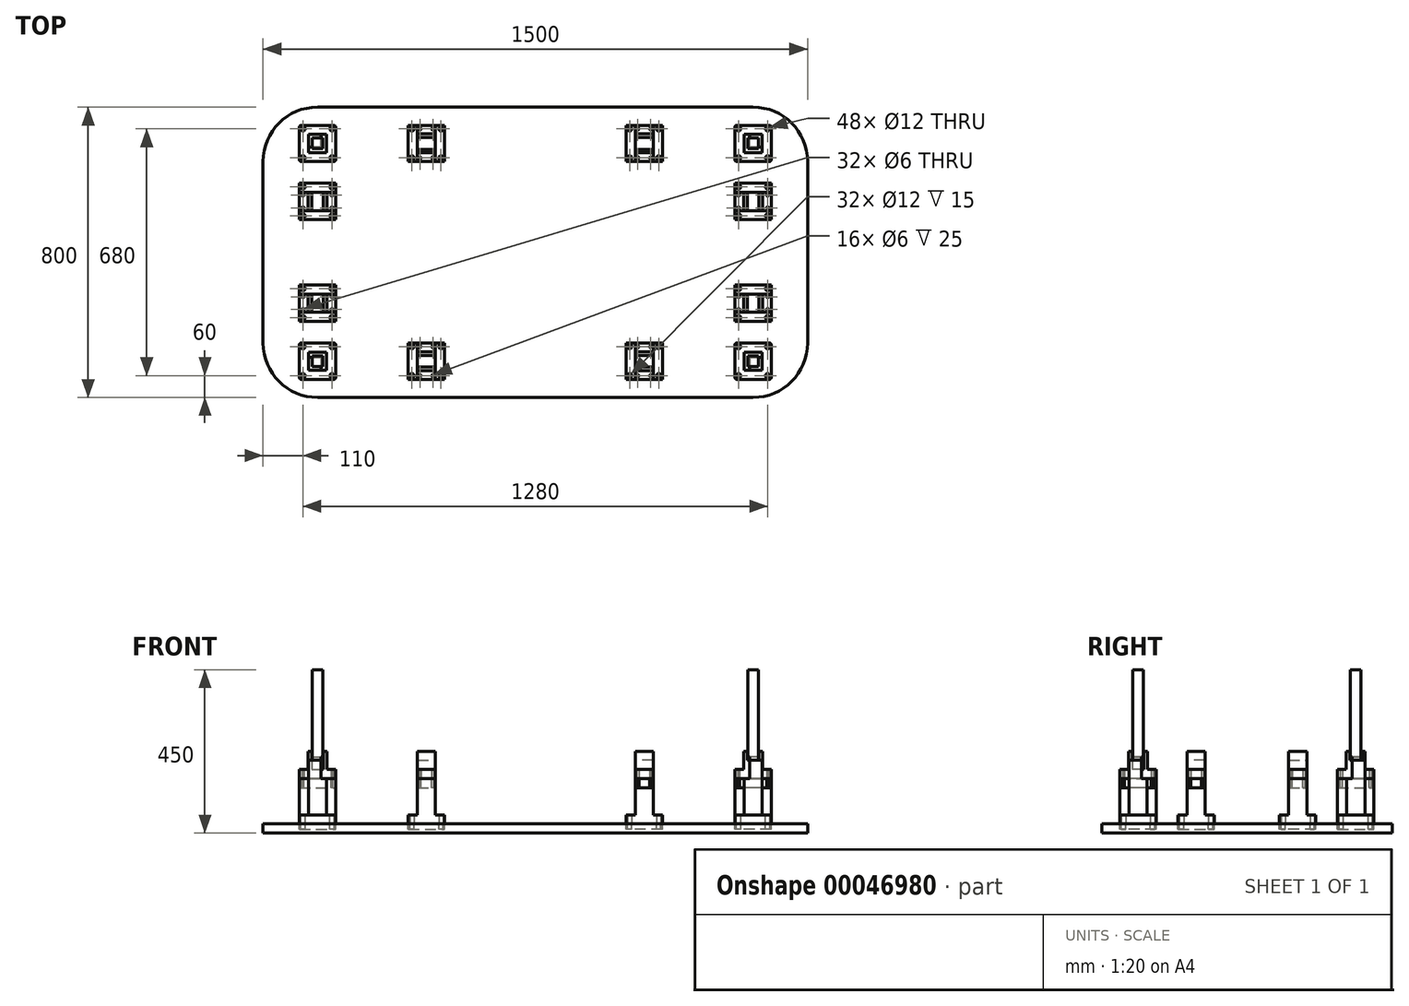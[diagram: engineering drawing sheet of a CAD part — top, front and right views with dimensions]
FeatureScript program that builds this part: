
annotation { "Feature Type Name" : "Feature", "Feature Type Description" : "" }
export const myFeature = defineFeature(function(context is Context, id is Id, definition is map)
    precondition{}
    {
        {
            var Q0;
            Q0=qCreatedBy(makeId("Top.planeOp"),FACE);
            var sketch = newSketch(context, id + "F0", { "sketchPlane" : qUnion([Q0])});
            skLineSegment(sketch, "E0.rect.bottom", {"start": v(-750, 400) * mm, "end": v(750, 400) * mm});
            skLineSegment(sketch, "E0.rect.top", {"start": v(-750, -400) * mm, "end": v(750, -400) * mm});
            skLineSegment(sketch, "E0.rect.left", {"start": v(-750, 400) * mm, "end": v(-750, -400) * mm});
            skLineSegment(sketch, "E0.rect.right", {"start": v(750, 400) * mm, "end": v(750, -400) * mm});
            skPoint(sketch, "E0.rect.middle", {"position": v(0, 0) * mm});
            skSolve(sketch);
        }
        {
            var Q0;
            Q0=qSketchRegion(id+"F0",true);
            extrude(context, id + "F1", {"entities" : qUnion([Q0]), "depth" : 25 * mm});
        }
        {
            var Q0;
            Q0=makeQuery(id+"F1.opExtrude","CAP_FACE",FACE,{"disambiguationData":[OSD([sQuery(id+"F0.wireOp",EDGE,"E0.rect.bottom"),sQuery(id+"F0.wireOp",EDGE,"E0.rect.top"),sQuery(id+"F0.wireOp",EDGE,"E0.rect.left"),sQuery(id+"F0.wireOp",EDGE,"E0.rect.right")])],"isStart":false});
            var sketch = newSketch(context, id + "F2", { "sketchPlane" : qUnion([Q0])});
            skLineSegment(sketch, "E1.rect.bottom", {"start": v(-600, 300) * mm, "end": v(600, 300) * mm, "construction": true});
            skLineSegment(sketch, "E1.rect.top", {"start": v(-600, -300) * mm, "end": v(600, -300) * mm, "construction": true});
            skLineSegment(sketch, "E1.rect.left", {"start": v(-600, 300) * mm, "end": v(-600, -300) * mm, "construction": true});
            skLineSegment(sketch, "E1.rect.right", {"start": v(600, 300) * mm, "end": v(600, -300) * mm, "construction": true});
            skPoint(sketch, "E1.rect.middle", {"position": v(0, 0) * mm});
            skLineSegment(sketch, "E2.rect.bottom", {"start": v(-650, 350) * mm, "end": v(-550, 350) * mm});
            skLineSegment(sketch, "E2.rect.top", {"start": v(-650, 250) * mm, "end": v(-550, 250) * mm});
            skLineSegment(sketch, "E2.rect.left", {"start": v(-650, 350) * mm, "end": v(-650, 250) * mm});
            skLineSegment(sketch, "E2.rect.right", {"start": v(-550, 350) * mm, "end": v(-550, 250) * mm});
            skPoint(sketch, "E2.rect.middle", {"position": v(-600, 300) * mm});
            skLineSegment(sketch, "E3.rect.bottom", {"start": v(550, 350) * mm, "end": v(650, 350) * mm});
            skLineSegment(sketch, "E3.rect.top", {"start": v(550, 250) * mm, "end": v(650, 250) * mm});
            skLineSegment(sketch, "E3.rect.left", {"start": v(550, 350) * mm, "end": v(550, 250) * mm});
            skLineSegment(sketch, "E3.rect.right", {"start": v(650, 350) * mm, "end": v(650, 250) * mm});
            skPoint(sketch, "E3.rect.middle", {"position": v(600, 300) * mm});
            skLineSegment(sketch, "E4.rect.bottom", {"start": v(-650, -250) * mm, "end": v(-550, -250) * mm});
            skLineSegment(sketch, "E4.rect.top", {"start": v(-650, -350) * mm, "end": v(-550, -350) * mm});
            skLineSegment(sketch, "E4.rect.left", {"start": v(-650, -250) * mm, "end": v(-650, -350) * mm});
            skLineSegment(sketch, "E4.rect.right", {"start": v(-550, -250) * mm, "end": v(-550, -350) * mm});
            skPoint(sketch, "E4.rect.middle", {"position": v(-600, -300) * mm});
            skLineSegment(sketch, "E5.rect.bottom", {"start": v(550, -250) * mm, "end": v(650, -250) * mm});
            skLineSegment(sketch, "E5.rect.top", {"start": v(550, -350) * mm, "end": v(650, -350) * mm});
            skLineSegment(sketch, "E5.rect.left", {"start": v(550, -250) * mm, "end": v(550, -350) * mm});
            skLineSegment(sketch, "E5.rect.right", {"start": v(650, -250) * mm, "end": v(650, -350) * mm});
            skPoint(sketch, "E5.rect.middle", {"position": v(600, -300) * mm});
            skSolve(sketch);
        }
        {
            var Q0;
            Q0=qSketchRegion(id+"F2",true);
            extrude(context, id + "F3", {"entities" : qUnion([Q0]), "depth" : 25 * mm});
        }
        {
            var Q0;
            Q0=makeQuery(id+"F3.opExtrude","SWEPT_EDGE",EDGE,{"disambiguationData":[OSD([sQuery(id+"F2.wireOp",EDGE,"E2.rect.top"),sQuery(id+"F2.wireOp",EDGE,"E2.rect.right")])]});
            var Q1;
            Q1=makeQuery(id+"F3.opExtrude","SWEPT_EDGE",EDGE,{"disambiguationData":[OSD([sQuery(id+"F2.wireOp",EDGE,"E2.rect.top"),sQuery(id+"F2.wireOp",EDGE,"E2.rect.left")])]});
            var Q2;
            Q2=makeQuery(id+"F3.opExtrude","SWEPT_EDGE",EDGE,{"disambiguationData":[OSD([sQuery(id+"F2.wireOp",EDGE,"E2.rect.bottom"),sQuery(id+"F2.wireOp",EDGE,"E2.rect.right")])]});
            var Q3;
            Q3=makeQuery(id+"F3.opExtrude","SWEPT_EDGE",EDGE,{"disambiguationData":[OSD([sQuery(id+"F2.wireOp",EDGE,"E2.rect.bottom"),sQuery(id+"F2.wireOp",EDGE,"E2.rect.left")])]});
            var Q4;
            Q4=makeQuery(id+"F3.opExtrude","SWEPT_EDGE",EDGE,{"disambiguationData":[OSD([sQuery(id+"F2.wireOp",EDGE,"E4.rect.bottom"),sQuery(id+"F2.wireOp",EDGE,"E4.rect.right")])]});
            var Q5;
            Q5=makeQuery(id+"F3.opExtrude","SWEPT_EDGE",EDGE,{"disambiguationData":[OSD([sQuery(id+"F2.wireOp",EDGE,"E4.rect.bottom"),sQuery(id+"F2.wireOp",EDGE,"E4.rect.left")])]});
            var Q6;
            Q6=makeQuery(id+"F3.opExtrude","SWEPT_EDGE",EDGE,{"disambiguationData":[OSD([sQuery(id+"F2.wireOp",EDGE,"E4.rect.top"),sQuery(id+"F2.wireOp",EDGE,"E4.rect.left")])]});
            var Q7;
            Q7=makeQuery(id+"F3.opExtrude","SWEPT_EDGE",EDGE,{"disambiguationData":[OSD([sQuery(id+"F2.wireOp",EDGE,"E4.rect.top"),sQuery(id+"F2.wireOp",EDGE,"E4.rect.right")])]});
            var Q8;
            Q8=makeQuery(id+"F3.opExtrude","SWEPT_EDGE",EDGE,{"disambiguationData":[OSD([sQuery(id+"F2.wireOp",EDGE,"E5.rect.bottom"),sQuery(id+"F2.wireOp",EDGE,"E5.rect.left")])]});
            var Q9;
            Q9=makeQuery(id+"F3.opExtrude","SWEPT_EDGE",EDGE,{"disambiguationData":[OSD([sQuery(id+"F2.wireOp",EDGE,"E5.rect.bottom"),sQuery(id+"F2.wireOp",EDGE,"E5.rect.right")])]});
            var Q10;
            Q10=makeQuery(id+"F3.opExtrude","SWEPT_EDGE",EDGE,{"disambiguationData":[OSD([sQuery(id+"F2.wireOp",EDGE,"E5.rect.top"),sQuery(id+"F2.wireOp",EDGE,"E5.rect.left")])]});
            var Q11;
            Q11=makeQuery(id+"F3.opExtrude","SWEPT_EDGE",EDGE,{"disambiguationData":[OSD([sQuery(id+"F2.wireOp",EDGE,"E5.rect.top"),sQuery(id+"F2.wireOp",EDGE,"E5.rect.right")])]});
            var Q12;
            Q12=makeQuery(id+"F3.opExtrude","SWEPT_EDGE",EDGE,{"disambiguationData":[OSD([sQuery(id+"F2.wireOp",EDGE,"E3.rect.top"),sQuery(id+"F2.wireOp",EDGE,"E3.rect.right")])]});
            var Q13;
            Q13=makeQuery(id+"F3.opExtrude","SWEPT_EDGE",EDGE,{"disambiguationData":[OSD([sQuery(id+"F2.wireOp",EDGE,"E3.rect.bottom"),sQuery(id+"F2.wireOp",EDGE,"E3.rect.right")])]});
            var Q14;
            Q14=makeQuery(id+"F3.opExtrude","SWEPT_EDGE",EDGE,{"disambiguationData":[OSD([sQuery(id+"F2.wireOp",EDGE,"E3.rect.bottom"),sQuery(id+"F2.wireOp",EDGE,"E3.rect.left")])]});
            var Q15;
            Q15=makeQuery(id+"F3.opExtrude","SWEPT_EDGE",EDGE,{"disambiguationData":[OSD([sQuery(id+"F2.wireOp",EDGE,"E3.rect.top"),sQuery(id+"F2.wireOp",EDGE,"E3.rect.left")])]});
            fillet(context, id + "F4", {"entities" : qUnion([Q0, Q1, Q2, Q3, Q4, Q5, Q6, Q7, Q8, Q9, Q10, Q11, Q12, Q13, Q14, Q15]), "radius" : 5 * mm, "tangentPropagation" : true, "allowEdgeOverflow" : false});
        }
        {
            var Q0;
            Q0=makeQuery(id+"F3.opExtrude","CAP_FACE",FACE,{"disambiguationData":[OSD([sQuery(id+"F2.wireOp",EDGE,"E2.rect.bottom"),sQuery(id+"F2.wireOp",EDGE,"E2.rect.top"),sQuery(id+"F2.wireOp",EDGE,"E2.rect.left"),sQuery(id+"F2.wireOp",EDGE,"E2.rect.right")])],"isStart":false});
            var sketch = newSketch(context, id + "F5", { "sketchPlane" : qUnion([Q0])});
            skLineSegment(sketch, "E6.rect.bottom", {"start": v(-640, 340) * mm, "end": v(-560, 340) * mm, "construction": true});
            skLineSegment(sketch, "E6.rect.top", {"start": v(-640, 260) * mm, "end": v(-560, 260) * mm, "construction": true});
            skLineSegment(sketch, "E6.rect.left", {"start": v(-640, 340) * mm, "end": v(-640, 260) * mm, "construction": true});
            skLineSegment(sketch, "E6.rect.right", {"start": v(-560, 340) * mm, "end": v(-560, 260) * mm, "construction": true});
            skPoint(sketch, "E6.rect.middle", {"position": v(-600, 300) * mm});
            skCircle(sketch, "E7", {"center": v(-640, 340) * mm, "radius": 6 * mm});
            skCircle(sketch, "E8", {"center": v(-560, 340) * mm, "radius": 6 * mm});
            skCircle(sketch, "E9", {"center": v(-640, 260) * mm, "radius": 6 * mm});
            skCircle(sketch, "E10", {"center": v(-560, 260) * mm, "radius": 6 * mm});
            skCircle(sketch, "E11.MirrorC", {"center": v(560, 260) * mm, "radius": 6 * mm});
            skCircle(sketch, "E12.MirrorC", {"center": v(640, 260) * mm, "radius": 6 * mm});
            skCircle(sketch, "E13.MirrorC", {"center": v(560, 340) * mm, "radius": 6 * mm});
            skCircle(sketch, "E14.MirrorC", {"center": v(640, 340) * mm, "radius": 6 * mm});
            skLineSegment(sketch, "E15.MirrorCS", {"start": v(640, 340) * mm, "end": v(560, 340) * mm, "construction": true});
            skLineSegment(sketch, "E16.MirrorCS", {"start": v(640, 260) * mm, "end": v(560, 260) * mm, "construction": true});
            skPoint(sketch, "E17.MirrorP", {"position": v(600, 300) * mm});
            skLineSegment(sketch, "E18.MirrorCS", {"start": v(560, 340) * mm, "end": v(560, 260) * mm, "construction": true});
            skLineSegment(sketch, "E19.MirrorCS", {"start": v(640, 340) * mm, "end": v(640, 260) * mm, "construction": true});
            skCircle(sketch, "E20.MirrorC", {"center": v(640, -340) * mm, "radius": 6 * mm});
            skCircle(sketch, "E21.MirrorC", {"center": v(560, -340) * mm, "radius": 6 * mm});
            skCircle(sketch, "E22.MirrorC", {"center": v(640, -260) * mm, "radius": 6 * mm});
            skCircle(sketch, "E23.MirrorC", {"center": v(560, -260) * mm, "radius": 6 * mm});
            skCircle(sketch, "E24.MirrorC", {"center": v(-560, -260) * mm, "radius": 6 * mm});
            skCircle(sketch, "E25.MirrorC", {"center": v(-640, -260) * mm, "radius": 6 * mm});
            skCircle(sketch, "E26.MirrorC", {"center": v(-560, -340) * mm, "radius": 6 * mm});
            skCircle(sketch, "E27.MirrorC", {"center": v(-640, -340) * mm, "radius": 6 * mm});
            skPoint(sketch, "E28.MirrorP", {"position": v(600, -300) * mm});
            skPoint(sketch, "E29.MirrorP", {"position": v(-600, -300) * mm});
            skLineSegment(sketch, "E30.MirrorCS", {"start": v(640, -340) * mm, "end": v(560, -340) * mm, "construction": true});
            skLineSegment(sketch, "E31.MirrorCS", {"start": v(640, -260) * mm, "end": v(560, -260) * mm, "construction": true});
            skLineSegment(sketch, "E32.MirrorCS", {"start": v(560, -340) * mm, "end": v(560, -260) * mm, "construction": true});
            skLineSegment(sketch, "E33.MirrorCS", {"start": v(640, -340) * mm, "end": v(640, -260) * mm, "construction": true});
            skLineSegment(sketch, "E34.MirrorCS", {"start": v(-640, -340) * mm, "end": v(-560, -340) * mm, "construction": true});
            skLineSegment(sketch, "E35.MirrorCS", {"start": v(-640, -260) * mm, "end": v(-560, -260) * mm, "construction": true});
            skLineSegment(sketch, "E36.MirrorCS", {"start": v(-640, -340) * mm, "end": v(-640, -260) * mm, "construction": true});
            skLineSegment(sketch, "E37.MirrorCS", {"start": v(-560, -340) * mm, "end": v(-560, -260) * mm, "construction": true});
            skLineSegment(sketch, "E38.MirrorCS", {"start": v(-640, 260) * mm, "end": v(-560, 260) * mm});
            skSolve(sketch);
        }
        {
            var Q0;
            Q0=qSketchRegion(id+"F5",true);
            extrude(context, id + "F6", {"entities" : qUnion([Q0]), "operationType" : NewBodyOperationType.REMOVE, "oppositeDirection" : true, "depth" : 40 * mm});
        }
        {
            var Q0;
            Q0=makeQuery(id+"F3.opExtrude","CAP_FACE",FACE,{"disambiguationData":[OSD([sQuery(id+"F2.wireOp",EDGE,"E2.rect.bottom"),sQuery(id+"F2.wireOp",EDGE,"E2.rect.top"),sQuery(id+"F2.wireOp",EDGE,"E2.rect.left"),sQuery(id+"F2.wireOp",EDGE,"E2.rect.right")])],"isStart":false});
            var sketch = newSketch(context, id + "F7", { "sketchPlane" : qUnion([Q0])});
            skLineSegment(sketch, "E39.rect.bottom", {"start": v(-625, 325) * mm, "end": v(-575, 325) * mm});
            skLineSegment(sketch, "E39.rect.top", {"start": v(-625, 275) * mm, "end": v(-575, 275) * mm});
            skLineSegment(sketch, "E39.rect.left", {"start": v(-625, 325) * mm, "end": v(-625, 275) * mm});
            skLineSegment(sketch, "E39.rect.right", {"start": v(-575, 325) * mm, "end": v(-575, 275) * mm});
            skPoint(sketch, "E39.rect.middle", {"position": v(-600, 300) * mm});
            skLineSegment(sketch, "E40.MirrorCS", {"start": v(625, 325) * mm, "end": v(625, 275) * mm});
            skLineSegment(sketch, "E41.MirrorCS", {"start": v(575, 325) * mm, "end": v(575, 275) * mm});
            skPoint(sketch, "E42.MirrorP", {"position": v(600, 300) * mm});
            skLineSegment(sketch, "E43.MirrorCS", {"start": v(625, 275) * mm, "end": v(575, 275) * mm});
            skLineSegment(sketch, "E44.MirrorCS", {"start": v(625, 325) * mm, "end": v(575, 325) * mm});
            skLineSegment(sketch, "E45.MirrorCS", {"start": v(-625, -275) * mm, "end": v(-575, -275) * mm});
            skLineSegment(sketch, "E46.MirrorCS", {"start": v(-625, -325) * mm, "end": v(-575, -325) * mm});
            skPoint(sketch, "E47.MirrorP", {"position": v(-600, -300) * mm});
            skLineSegment(sketch, "E48.MirrorCS", {"start": v(-625, -325) * mm, "end": v(-625, -275) * mm});
            skLineSegment(sketch, "E49.MirrorCS", {"start": v(-575, -325) * mm, "end": v(-575, -275) * mm});
            skPoint(sketch, "E50.MirrorP", {"position": v(600, -300) * mm});
            skLineSegment(sketch, "E51.MirrorCS", {"start": v(625, -325) * mm, "end": v(625, -275) * mm});
            skLineSegment(sketch, "E52.MirrorCS", {"start": v(575, -325) * mm, "end": v(575, -275) * mm});
            skLineSegment(sketch, "E53.MirrorCS", {"start": v(625, -275) * mm, "end": v(575, -275) * mm});
            skLineSegment(sketch, "E54.MirrorCS", {"start": v(625, -325) * mm, "end": v(575, -325) * mm});
            skSolve(sketch);
        }
        {
            var Q0;
            Q0=qSketchRegion(id+"F7",true);
            extrude(context, id + "F8", {"entities" : qUnion([Q0]), "operationType" : NewBodyOperationType.ADD, "depth" : 150 * mm});
        }
        {
            var Q0;
            Q0=makeQuery(id+"F8.opExtrude","CAP_FACE",FACE,{"disambiguationData":[OSD([sQuery(id+"F7.wireOp",EDGE,"E39.rect.bottom"),sQuery(id+"F7.wireOp",EDGE,"E39.rect.top"),sQuery(id+"F7.wireOp",EDGE,"E39.rect.left"),sQuery(id+"F7.wireOp",EDGE,"E39.rect.right")])],"isStart":false});
            var sketch = newSketch(context, id + "F9", { "sketchPlane" : qUnion([Q0])});
            skLineSegment(sketch, "E55.rect.bottom", {"start": v(-614.75, 314.75) * mm, "end": v(-585.25, 314.75) * mm});
            skLineSegment(sketch, "E55.rect.top", {"start": v(-614.75, 285.25) * mm, "end": v(-585.25, 285.25) * mm});
            skLineSegment(sketch, "E55.rect.left", {"start": v(-614.75, 314.75) * mm, "end": v(-614.75, 285.25) * mm});
            skLineSegment(sketch, "E55.rect.right", {"start": v(-585.25, 314.75) * mm, "end": v(-585.25, 285.25) * mm});
            skPoint(sketch, "E55.rect.middle", {"position": v(-600, 300) * mm});
            skLineSegment(sketch, "E56.MirrorCS", {"start": v(614.75, 314.75) * mm, "end": v(614.75, 285.25) * mm});
            skLineSegment(sketch, "E57.MirrorCS", {"start": v(614.75, 285.25) * mm, "end": v(585.25, 285.25) * mm});
            skLineSegment(sketch, "E58.MirrorCS", {"start": v(614.75, 314.75) * mm, "end": v(585.25, 314.75) * mm});
            skPoint(sketch, "E59.MirrorP", {"position": v(600, 300) * mm});
            skLineSegment(sketch, "E60.MirrorCS", {"start": v(585.25, 314.75) * mm, "end": v(585.25, 285.25) * mm});
            skLineSegment(sketch, "E61.MirrorCS", {"start": v(-614.75, -314.75) * mm, "end": v(-614.75, -285.25) * mm});
            skLineSegment(sketch, "E62.MirrorCS", {"start": v(-614.75, -285.25) * mm, "end": v(-585.25, -285.25) * mm});
            skLineSegment(sketch, "E63.MirrorCS", {"start": v(-614.75, -314.75) * mm, "end": v(-585.25, -314.75) * mm});
            skPoint(sketch, "E64.MirrorP", {"position": v(-600, -300) * mm});
            skLineSegment(sketch, "E65.MirrorCS", {"start": v(-585.25, -314.75) * mm, "end": v(-585.25, -285.25) * mm});
            skLineSegment(sketch, "E66.MirrorCS", {"start": v(614.75, -314.75) * mm, "end": v(614.75, -285.25) * mm});
            skLineSegment(sketch, "E67.MirrorCS", {"start": v(614.75, -285.25) * mm, "end": v(585.25, -285.25) * mm});
            skLineSegment(sketch, "E68.MirrorCS", {"start": v(614.75, -314.75) * mm, "end": v(585.25, -314.75) * mm});
            skLineSegment(sketch, "E69.MirrorCS", {"start": v(585.25, -314.75) * mm, "end": v(585.25, -285.25) * mm});
            skPoint(sketch, "E70.MirrorP", {"position": v(600, -300) * mm});
            skSolve(sketch);
        }
        {
            var Q0;
            Q0=makeQuery(id+"F8.opExtrude","CAP_FACE",FACE,{"disambiguationData":[OSD([sQuery(id+"F7.wireOp",EDGE,"E39.rect.bottom"),sQuery(id+"F7.wireOp",EDGE,"E39.rect.top"),sQuery(id+"F7.wireOp",EDGE,"E39.rect.left"),sQuery(id+"F7.wireOp",EDGE,"E39.rect.right")])],"isStart":false});
            var sketch = newSketch(context, id + "F10", { "sketchPlane" : qUnion([Q0])});
            skLineSegment(sketch, "E71", {"start": v(-575, 275) * mm, "end": v(-575, 290) * mm});
            skLineSegment(sketch, "E72.MirrorCS", {"start": v(575, 290) * mm, "end": v(585.25, 290) * mm});
            skLineSegment(sketch, "E73.MirrorCS", {"start": v(585.25, 275) * mm, "end": v(575, 275) * mm});
            skLineSegment(sketch, "E74.MirrorCS", {"start": v(575, 275) * mm, "end": v(575, 290) * mm});
            skLineSegment(sketch, "E75.MirrorCS", {"start": v(585.25, 290) * mm, "end": v(585.25, 275) * mm});
            skLineSegment(sketch, "E76.MirrorCS", {"start": v(-575, -275) * mm, "end": v(-575, -290) * mm});
            skLineSegment(sketch, "E77.MirrorCS", {"start": v(-575, -290) * mm, "end": v(-585.25, -290) * mm});
            skLineSegment(sketch, "E78.MirrorCS", {"start": v(585.25, -275) * mm, "end": v(575, -275) * mm});
            skLineSegment(sketch, "E79.MirrorCS", {"start": v(585.25, -290) * mm, "end": v(585.25, -275) * mm});
            skLineSegment(sketch, "E80.MirrorCS", {"start": v(575, -275) * mm, "end": v(575, -290) * mm});
            skLineSegment(sketch, "E81.MirrorCS", {"start": v(575, -290) * mm, "end": v(585.25, -290) * mm});
            skLineSegment(sketch, "E82", {"start": v(-575, 290) * mm, "end": v(-625, 290) * mm});
            skLineSegment(sketch, "E83", {"start": v(-625, 290) * mm, "end": v(-625, 275) * mm});
            skLineSegment(sketch, "E84", {"start": v(-625, 275) * mm, "end": v(-575, 275) * mm});
            skLineSegment(sketch, "E85.MirrorCS", {"start": v(625, 290) * mm, "end": v(625, 275) * mm});
            skLineSegment(sketch, "E86.MirrorCS", {"start": v(575, 290) * mm, "end": v(625, 290) * mm});
            skLineSegment(sketch, "E87.MirrorCS", {"start": v(625, 275) * mm, "end": v(575, 275) * mm});
            skLineSegment(sketch, "E88.MirrorCS", {"start": v(625, -290) * mm, "end": v(625, -275) * mm});
            skLineSegment(sketch, "E89.MirrorCS", {"start": v(-625, -290) * mm, "end": v(-625, -275) * mm});
            skLineSegment(sketch, "E90.MirrorCS", {"start": v(-575, -290) * mm, "end": v(-625, -290) * mm});
            skLineSegment(sketch, "E91.MirrorCS", {"start": v(-625, -275) * mm, "end": v(-575, -275) * mm});
            skLineSegment(sketch, "E92.MirrorCS", {"start": v(575, -290) * mm, "end": v(625, -290) * mm});
            skLineSegment(sketch, "E93.MirrorCS", {"start": v(625, -275) * mm, "end": v(575, -275) * mm});
            skSolve(sketch);
        }
        {
            var Q0;
            Q0=qSketchRegion(id+"F9",true);
            extrude(context, id + "F11", {"entities" : qUnion([Q0]), "operationType" : NewBodyOperationType.ADD, "depth" : 250 * mm});
        }
        {
            var Q0;
            Q0=qSketchRegion(id+"F10",true);
            extrude(context, id + "F12", {"entities" : qUnion([Q0]), "operationType" : NewBodyOperationType.REMOVE, "oppositeDirection" : true, "depth" : 50 * mm});
        }
        {
            var Q0;
            Q0=makeQuery(id+"F11.opExtrude","SWEPT_FACE",FACE,{"disambiguationData":[OSD([sQuery(id+"F9.wireOp",EDGE,"E55.rect.top")])]});
            var sketch = newSketch(context, id + "F13", { "sketchPlane" : qUnion([Q0])});
            skLineSegment(sketch, "E94.bottom", {"start": v(-614.75, 200) * mm, "end": v(-585.25, 200) * mm});
            skLineSegment(sketch, "E94.top", {"start": v(-614.75, 210) * mm, "end": v(-585.25, 210) * mm});
            skLineSegment(sketch, "E94.left", {"start": v(-614.75, 200) * mm, "end": v(-614.75, 210) * mm});
            skLineSegment(sketch, "E94.right", {"start": v(-585.25, 200) * mm, "end": v(-585.25, 210) * mm});
            skLineSegment(sketch, "E95.MirrorCS", {"start": v(614.75, 210) * mm, "end": v(585.25, 210) * mm});
            skLineSegment(sketch, "E96.MirrorCS", {"start": v(585.25, 200) * mm, "end": v(585.25, 210) * mm});
            skLineSegment(sketch, "E97.MirrorCS", {"start": v(614.75, 200) * mm, "end": v(614.75, 210) * mm});
            skLineSegment(sketch, "E98.MirrorCS", {"start": v(614.75, 200) * mm, "end": v(585.25, 200) * mm});
            skSolve(sketch);
        }
        {
            var Q0;
            Q0=qSketchRegion(id+"F13",true);
            extrude(context, id + "F14", {"entities" : qUnion([Q0]), "operationType" : NewBodyOperationType.REMOVE, "oppositeDirection" : true, "depth" : 4.75 * mm});
        }
        {
            var Q0;
            Q0=makeQuery(id+"F11.opExtrude","SWEPT_FACE",FACE,{"disambiguationData":[OSD([sQuery(id+"F9.wireOp",EDGE,"E67.MirrorCS")])]});
            var sketch = newSketch(context, id + "F15", { "sketchPlane" : qUnion([Q0])});
            skLineSegment(sketch, "E99.bottom", {"start": v(-614.75, 200) * mm, "end": v(-585.25, 200) * mm});
            skLineSegment(sketch, "E99.top", {"start": v(-614.75, 210) * mm, "end": v(-585.25, 210) * mm});
            skLineSegment(sketch, "E99.left", {"start": v(-614.75, 200) * mm, "end": v(-614.75, 210) * mm});
            skLineSegment(sketch, "E99.right", {"start": v(-585.25, 200) * mm, "end": v(-585.25, 210) * mm});
            skLineSegment(sketch, "E100.MirrorCS", {"start": v(614.75, 210) * mm, "end": v(585.25, 210) * mm});
            skLineSegment(sketch, "E101.MirrorCS", {"start": v(585.25, 200) * mm, "end": v(585.25, 210) * mm});
            skLineSegment(sketch, "E102.MirrorCS", {"start": v(614.75, 200) * mm, "end": v(614.75, 210) * mm});
            skLineSegment(sketch, "E103.MirrorCS", {"start": v(614.75, 200) * mm, "end": v(585.25, 200) * mm});
            skSolve(sketch);
        }
        {
            var Q0;
            Q0=qSketchRegion(id+"F15",true);
            extrude(context, id + "F16", {"entities" : qUnion([Q0]), "operationType" : NewBodyOperationType.REMOVE, "oppositeDirection" : true, "depth" : 4.75 * mm});
        }
        {
            var Q0;
            Q0=makeQuery(id+"F8.opExtrude","SWEPT_FACE",FACE,{"disambiguationData":[OSD([sQuery(id+"F7.wireOp",EDGE,"E39.rect.right")])]});
            var sketch = newSketch(context, id + "F17", { "sketchPlane" : qUnion([Q0])});
            skLineSegment(sketch, "E104", {"start": v(290, 150) * mm, "end": v(325, 150) * mm});
            skLineSegment(sketch, "E105", {"start": v(325, 150) * mm, "end": v(325, 200) * mm});
            skLineSegment(sketch, "E106", {"start": v(325, 200) * mm, "end": v(290, 200) * mm});
            skLineSegment(sketch, "E107", {"start": v(290, 200) * mm, "end": v(290, 150) * mm});
            skLineSegment(sketch, "E108.MirrorCS", {"start": v(-325, 200) * mm, "end": v(-290, 200) * mm});
            skLineSegment(sketch, "E109.MirrorCS", {"start": v(-325, 150) * mm, "end": v(-325, 200) * mm});
            skLineSegment(sketch, "E110.MirrorCS", {"start": v(-290, 200) * mm, "end": v(-290, 150) * mm});
            skLineSegment(sketch, "E111.MirrorCS", {"start": v(-290, 150) * mm, "end": v(-325, 150) * mm});
            skSolve(sketch);
        }
        {
            var Q0;
            Q0=qSketchRegion(id+"F17",true);
            extrude(context, id + "F18", {"entities" : qUnion([Q0]), "operationType" : NewBodyOperationType.REMOVE, "oppositeDirection" : true, "depth" : 15 * mm});
        }
        {
            var Q0;
            Q0=makeQuery(id+"F11.opExtrude","SWEPT_FACE",FACE,{"disambiguationData":[OSD([sQuery(id+"F9.wireOp",EDGE,"E55.rect.right")])]});
            var sketch = newSketch(context, id + "F19", { "sketchPlane" : qUnion([Q0])});
            skLineSegment(sketch, "E112", {"start": v(290, 210) * mm, "end": v(314.75, 210) * mm});
            skLineSegment(sketch, "E113", {"start": v(314.75, 210) * mm, "end": v(314.75, 200) * mm});
            skLineSegment(sketch, "E114", {"start": v(314.75, 200) * mm, "end": v(290, 200) * mm});
            skLineSegment(sketch, "E115", {"start": v(290, 200) * mm, "end": v(290, 210) * mm});
            skLineSegment(sketch, "E116.MirrorCS", {"start": v(-290, 200) * mm, "end": v(-290, 210) * mm});
            skLineSegment(sketch, "E117.MirrorCS", {"start": v(-314.75, 210) * mm, "end": v(-314.75, 200) * mm});
            skLineSegment(sketch, "E118.MirrorCS", {"start": v(-290, 210) * mm, "end": v(-314.75, 210) * mm});
            skLineSegment(sketch, "E119.MirrorCS", {"start": v(-314.75, 200) * mm, "end": v(-290, 200) * mm});
            skSolve(sketch);
        }
        {
            var Q0;
            Q0=qSketchRegion(id+"F19",true);
            extrude(context, id + "F20", {"entities" : qUnion([Q0]), "operationType" : NewBodyOperationType.REMOVE, "oppositeDirection" : true, "depth" : 4.75 * mm});
        }
        {
            var Q0;
            Q0=makeQuery(id+"F8.opExtrude","SWEPT_FACE",FACE,{"disambiguationData":[OSD([sQuery(id+"F7.wireOp",EDGE,"E52.MirrorCS")])]});
            var sketch = newSketch(context, id + "F21", { "sketchPlane" : qUnion([Q0])});
            skLineSegment(sketch, "E120", {"start": v(290, 150) * mm, "end": v(325, 150) * mm});
            skLineSegment(sketch, "E121", {"start": v(325, 150) * mm, "end": v(325, 200) * mm});
            skLineSegment(sketch, "E122", {"start": v(325, 200) * mm, "end": v(290, 200) * mm});
            skLineSegment(sketch, "E123", {"start": v(290, 200) * mm, "end": v(290, 150) * mm});
            skLineSegment(sketch, "E124.MirrorCS", {"start": v(-325, 200) * mm, "end": v(-290, 200) * mm});
            skLineSegment(sketch, "E125.MirrorCS", {"start": v(-325, 150) * mm, "end": v(-325, 200) * mm});
            skLineSegment(sketch, "E126.MirrorCS", {"start": v(-290, 200) * mm, "end": v(-290, 150) * mm});
            skLineSegment(sketch, "E127.MirrorCS", {"start": v(-290, 150) * mm, "end": v(-325, 150) * mm});
            skSolve(sketch);
        }
        {
            var Q0;
            Q0=qSketchRegion(id+"F21",true);
            extrude(context, id + "F22", {"entities" : qUnion([Q0]), "operationType" : NewBodyOperationType.REMOVE, "oppositeDirection" : true, "depth" : 15 * mm});
        }
        {
            var Q0;
            Q0=makeQuery(id+"F11.opExtrude","SWEPT_FACE",FACE,{"disambiguationData":[OSD([sQuery(id+"F9.wireOp",EDGE,"E69.MirrorCS")])]});
            var sketch = newSketch(context, id + "F23", { "sketchPlane" : qUnion([Q0])});
            skLineSegment(sketch, "E128", {"start": v(290, 210) * mm, "end": v(314.75, 210) * mm});
            skLineSegment(sketch, "E129", {"start": v(314.75, 210) * mm, "end": v(314.75, 200) * mm});
            skLineSegment(sketch, "E130", {"start": v(314.75, 200) * mm, "end": v(290, 200) * mm});
            skLineSegment(sketch, "E131", {"start": v(290, 200) * mm, "end": v(290, 210) * mm});
            skLineSegment(sketch, "E132.MirrorCS", {"start": v(-290, 200) * mm, "end": v(-290, 210) * mm});
            skLineSegment(sketch, "E133.MirrorCS", {"start": v(-314.75, 210) * mm, "end": v(-314.75, 200) * mm});
            skLineSegment(sketch, "E134.MirrorCS", {"start": v(-290, 210) * mm, "end": v(-314.75, 210) * mm});
            skLineSegment(sketch, "E135.MirrorCS", {"start": v(-314.75, 200) * mm, "end": v(-290, 200) * mm});
            skSolve(sketch);
        }
        {
            var Q0;
            Q0=qSketchRegion(id+"F23",true);
            extrude(context, id + "F24", {"entities" : qUnion([Q0]), "operationType" : NewBodyOperationType.REMOVE, "oppositeDirection" : true, "depth" : 4.75 * mm});
        }
        {
            var Q0;
            Q0=makeQuery(id+"F1.opExtrude","CAP_FACE",FACE,{"disambiguationData":[OSD([sQuery(id+"F0.wireOp",EDGE,"E0.rect.bottom"),sQuery(id+"F0.wireOp",EDGE,"E0.rect.top"),sQuery(id+"F0.wireOp",EDGE,"E0.rect.left"),sQuery(id+"F0.wireOp",EDGE,"E0.rect.right")])],"isStart":false});
            var sketch = newSketch(context, id + "F25", { "sketchPlane" : qUnion([Q0])});
            skLineSegment(sketch, "E136", {"start": v(-599.44, -250) * mm, "end": v(617.98, -250) * mm, "construction": true});
            skLineSegment(sketch, "E137", {"start": v(-601.09, -350) * mm, "end": v(606.16, -350) * mm, "construction": true});
            skLineSegment(sketch, "E138", {"start": v(-650, 282.76) * mm, "end": v(-650, -296.2) * mm, "construction": true});
            skLineSegment(sketch, "E139", {"start": v(-550, 281.52) * mm, "end": v(-550, -298.7) * mm, "construction": true});
            skLineSegment(sketch, "E140.bottom", {"start": v(-650, 190) * mm, "end": v(-550, 190) * mm});
            skLineSegment(sketch, "E140.top", {"start": v(-650, 90) * mm, "end": v(-550, 90) * mm});
            skLineSegment(sketch, "E140.left", {"start": v(-650, 190) * mm, "end": v(-650, 90) * mm});
            skLineSegment(sketch, "E140.right", {"start": v(-550, 190) * mm, "end": v(-550, 90) * mm});
            skLineSegment(sketch, "E141.bottom", {"start": v(-350, -250) * mm, "end": v(-250, -250) * mm});
            skLineSegment(sketch, "E141.top", {"start": v(-350, -350) * mm, "end": v(-250, -350) * mm});
            skLineSegment(sketch, "E141.left", {"start": v(-350, -250) * mm, "end": v(-350, -350) * mm});
            skLineSegment(sketch, "E141.right", {"start": v(-250, -250) * mm, "end": v(-250, -350) * mm});
            skLineSegment(sketch, "E142.MirrorCS", {"start": v(-650, -190) * mm, "end": v(-550, -190) * mm});
            skLineSegment(sketch, "E143.MirrorCS", {"start": v(-650, -190) * mm, "end": v(-650, -90) * mm});
            skLineSegment(sketch, "E144.MirrorCS", {"start": v(-550, -190) * mm, "end": v(-550, -90) * mm});
            skLineSegment(sketch, "E145.MirrorCS", {"start": v(-650, -90) * mm, "end": v(-550, -90) * mm});
            skLineSegment(sketch, "E146.MirrorCS", {"start": v(650, 190) * mm, "end": v(550, 190) * mm});
            skLineSegment(sketch, "E147.MirrorCS", {"start": v(650, 190) * mm, "end": v(650, 90) * mm});
            skLineSegment(sketch, "E148.MirrorCS", {"start": v(550, 190) * mm, "end": v(550, 90) * mm});
            skLineSegment(sketch, "E149.MirrorCS", {"start": v(650, 90) * mm, "end": v(550, 90) * mm});
            skLineSegment(sketch, "E150.MirrorCS", {"start": v(650, -90) * mm, "end": v(550, -90) * mm});
            skLineSegment(sketch, "E151.MirrorCS", {"start": v(550, -190) * mm, "end": v(550, -90) * mm});
            skLineSegment(sketch, "E152.MirrorCS", {"start": v(650, -190) * mm, "end": v(650, -90) * mm});
            skLineSegment(sketch, "E153.MirrorCS", {"start": v(650, -190) * mm, "end": v(550, -190) * mm});
            skLineSegment(sketch, "E154.MirrorCS", {"start": v(350, -250) * mm, "end": v(250, -250) * mm});
            skLineSegment(sketch, "E155.MirrorCS", {"start": v(250, -250) * mm, "end": v(250, -350) * mm});
            skLineSegment(sketch, "E156.MirrorCS", {"start": v(350, -250) * mm, "end": v(350, -350) * mm});
            skLineSegment(sketch, "E157.MirrorCS", {"start": v(350, -350) * mm, "end": v(250, -350) * mm});
            skLineSegment(sketch, "E158.MirrorCS", {"start": v(350, 250) * mm, "end": v(250, 250) * mm});
            skLineSegment(sketch, "E159.MirrorCS", {"start": v(-350, 250) * mm, "end": v(-250, 250) * mm});
            skLineSegment(sketch, "E160.MirrorCS", {"start": v(350, 250) * mm, "end": v(350, 350) * mm});
            skLineSegment(sketch, "E161.MirrorCS", {"start": v(250, 250) * mm, "end": v(250, 350) * mm});
            skLineSegment(sketch, "E162.MirrorCS", {"start": v(-250, 250) * mm, "end": v(-250, 350) * mm});
            skLineSegment(sketch, "E163.MirrorCS", {"start": v(-350, 250) * mm, "end": v(-350, 350) * mm});
            skLineSegment(sketch, "E164.MirrorCS", {"start": v(350, 350) * mm, "end": v(250, 350) * mm});
            skLineSegment(sketch, "E165.MirrorCS", {"start": v(-350, 350) * mm, "end": v(-250, 350) * mm});
            skLineSegment(sketch, "E166", {"start": v(-550, 190) * mm, "end": v(-650, 90) * mm, "construction": true});
            skLineSegment(sketch, "E167", {"start": v(-650, 190) * mm, "end": v(-550, 90) * mm, "construction": true});
            skLineSegment(sketch, "E168.rect.bottom", {"start": v(-640, 100) * mm, "end": v(-560, 100) * mm, "construction": true});
            skLineSegment(sketch, "E168.rect.top", {"start": v(-640, 180) * mm, "end": v(-560, 180) * mm, "construction": true});
            skLineSegment(sketch, "E168.rect.left", {"start": v(-640, 100) * mm, "end": v(-640, 180) * mm, "construction": true});
            skLineSegment(sketch, "E168.rect.right", {"start": v(-560, 100) * mm, "end": v(-560, 180) * mm, "construction": true});
            skPoint(sketch, "E168.rect.middle", {"position": v(-600, 140) * mm});
            skCircle(sketch, "E169", {"center": v(-640, 180) * mm, "radius": 6 * mm});
            skCircle(sketch, "E170", {"center": v(-560, 180) * mm, "radius": 6 * mm});
            skCircle(sketch, "E171", {"center": v(-640, 100) * mm, "radius": 6 * mm});
            skCircle(sketch, "E172", {"center": v(-560, 100) * mm, "radius": 6 * mm});
            skCircle(sketch, "E173.MirrorC", {"center": v(-560, -180) * mm, "radius": 6 * mm});
            skCircle(sketch, "E174.MirrorC", {"center": v(-640, -180) * mm, "radius": 6 * mm});
            skCircle(sketch, "E175.MirrorC", {"center": v(-560, -100) * mm, "radius": 6 * mm});
            skCircle(sketch, "E176.MirrorC", {"center": v(-640, -100) * mm, "radius": 6 * mm});
            skLineSegment(sketch, "E177.MirrorCS", {"start": v(-640, -180) * mm, "end": v(-560, -180) * mm, "construction": true});
            skPoint(sketch, "E178.MirrorP", {"position": v(-600, -140) * mm});
            skLineSegment(sketch, "E179.MirrorCS", {"start": v(-560, -100) * mm, "end": v(-560, -180) * mm, "construction": true});
            skLineSegment(sketch, "E180.MirrorCS", {"start": v(-640, -100) * mm, "end": v(-640, -180) * mm, "construction": true});
            skLineSegment(sketch, "E181.MirrorCS", {"start": v(-650, -190) * mm, "end": v(-550, -90) * mm, "construction": true});
            skLineSegment(sketch, "E182.MirrorCS", {"start": v(-550, -190) * mm, "end": v(-650, -90) * mm, "construction": true});
            skLineSegment(sketch, "E183.MirrorCS", {"start": v(-640, -100) * mm, "end": v(-560, -100) * mm, "construction": true});
            skCircle(sketch, "E184.MirrorC", {"center": v(560, 180) * mm, "radius": 6 * mm});
            skCircle(sketch, "E185.MirrorC", {"center": v(640, 180) * mm, "radius": 6 * mm});
            skCircle(sketch, "E186.MirrorC", {"center": v(640, 100) * mm, "radius": 6 * mm});
            skCircle(sketch, "E187.MirrorC", {"center": v(560, 100) * mm, "radius": 6 * mm});
            skCircle(sketch, "E188.MirrorC", {"center": v(640, -100) * mm, "radius": 6 * mm});
            skCircle(sketch, "E189.MirrorC", {"center": v(560, -100) * mm, "radius": 6 * mm});
            skCircle(sketch, "E190.MirrorC", {"center": v(560, -180) * mm, "radius": 6 * mm});
            skCircle(sketch, "E191.MirrorC", {"center": v(640, -180) * mm, "radius": 6 * mm});
            skLineSegment(sketch, "E192.MirrorCS", {"start": v(640, 180) * mm, "end": v(560, 180) * mm, "construction": true});
            skPoint(sketch, "E193.MirrorP", {"position": v(600, 140) * mm});
            skLineSegment(sketch, "E194.MirrorCS", {"start": v(560, 100) * mm, "end": v(560, 180) * mm, "construction": true});
            skLineSegment(sketch, "E195.MirrorCS", {"start": v(550, 190) * mm, "end": v(650, 90) * mm, "construction": true});
            skLineSegment(sketch, "E196.MirrorCS", {"start": v(640, 100) * mm, "end": v(640, 180) * mm, "construction": true});
            skLineSegment(sketch, "E197.MirrorCS", {"start": v(650, 190) * mm, "end": v(550, 90) * mm, "construction": true});
            skLineSegment(sketch, "E198.MirrorCS", {"start": v(640, 100) * mm, "end": v(560, 100) * mm, "construction": true});
            skLineSegment(sketch, "E199.MirrorCS", {"start": v(640, -100) * mm, "end": v(560, -100) * mm, "construction": true});
            skPoint(sketch, "E200.MirrorP", {"position": v(600, -140) * mm});
            skLineSegment(sketch, "E201.MirrorCS", {"start": v(560, -100) * mm, "end": v(560, -180) * mm, "construction": true});
            skLineSegment(sketch, "E202.MirrorCS", {"start": v(640, -100) * mm, "end": v(640, -180) * mm, "construction": true});
            skLineSegment(sketch, "E203.MirrorCS", {"start": v(650, -190) * mm, "end": v(550, -90) * mm, "construction": true});
            skLineSegment(sketch, "E204.MirrorCS", {"start": v(550, -190) * mm, "end": v(650, -90) * mm, "construction": true});
            skLineSegment(sketch, "E205.MirrorCS", {"start": v(640, -180) * mm, "end": v(560, -180) * mm, "construction": true});
            skLineSegment(sketch, "E206", {"start": v(-350, 350) * mm, "end": v(-250, 250) * mm, "construction": true});
            skLineSegment(sketch, "E207", {"start": v(-250, 350) * mm, "end": v(-350, 250) * mm, "construction": true});
            skLineSegment(sketch, "E208.rect.bottom", {"start": v(-340, 260) * mm, "end": v(-260, 260) * mm, "construction": true});
            skLineSegment(sketch, "E208.rect.top", {"start": v(-340, 340) * mm, "end": v(-260, 340) * mm, "construction": true});
            skLineSegment(sketch, "E208.rect.left", {"start": v(-340, 260) * mm, "end": v(-340, 340) * mm, "construction": true});
            skLineSegment(sketch, "E208.rect.right", {"start": v(-260, 260) * mm, "end": v(-260, 340) * mm, "construction": true});
            skPoint(sketch, "E208.rect.middle", {"position": v(-300, 300) * mm});
            skCircle(sketch, "E209", {"center": v(-340, 340) * mm, "radius": 6 * mm});
            skCircle(sketch, "E210", {"center": v(-260, 340) * mm, "radius": 6 * mm});
            skCircle(sketch, "E211", {"center": v(-340, 260) * mm, "radius": 6 * mm});
            skCircle(sketch, "E212", {"center": v(-260, 260) * mm, "radius": 6 * mm});
            skCircle(sketch, "E213.MirrorC", {"center": v(260, 340) * mm, "radius": 6 * mm});
            skCircle(sketch, "E214.MirrorC", {"center": v(340, 340) * mm, "radius": 6 * mm});
            skCircle(sketch, "E215.MirrorC", {"center": v(260, 260) * mm, "radius": 6 * mm});
            skCircle(sketch, "E216.MirrorC", {"center": v(340, 260) * mm, "radius": 6 * mm});
            skLineSegment(sketch, "E217.MirrorCS", {"start": v(340, 340) * mm, "end": v(260, 340) * mm, "construction": true});
            skLineSegment(sketch, "E218.MirrorCS", {"start": v(260, 260) * mm, "end": v(260, 340) * mm, "construction": true});
            skPoint(sketch, "E219.MirrorP", {"position": v(300, 300) * mm});
            skLineSegment(sketch, "E220.MirrorCS", {"start": v(340, 260) * mm, "end": v(340, 340) * mm, "construction": true});
            skLineSegment(sketch, "E221.MirrorCS", {"start": v(350, 350) * mm, "end": v(250, 250) * mm, "construction": true});
            skLineSegment(sketch, "E222.MirrorCS", {"start": v(250, 350) * mm, "end": v(350, 250) * mm, "construction": true});
            skLineSegment(sketch, "E223.MirrorCS", {"start": v(340, 260) * mm, "end": v(260, 260) * mm, "construction": true});
            skCircle(sketch, "E224.MirrorC", {"center": v(340, -340) * mm, "radius": 6 * mm});
            skCircle(sketch, "E225.MirrorC", {"center": v(260, -340) * mm, "radius": 6 * mm});
            skCircle(sketch, "E226.MirrorC", {"center": v(-260, -340) * mm, "radius": 6 * mm});
            skCircle(sketch, "E227.MirrorC", {"center": v(-340, -340) * mm, "radius": 6 * mm});
            skCircle(sketch, "E228.MirrorC", {"center": v(340, -260) * mm, "radius": 6 * mm});
            skCircle(sketch, "E229.MirrorC", {"center": v(260, -260) * mm, "radius": 6 * mm});
            skCircle(sketch, "E230.MirrorC", {"center": v(-260, -260) * mm, "radius": 6 * mm});
            skCircle(sketch, "E231.MirrorC", {"center": v(-340, -260) * mm, "radius": 6 * mm});
            skLineSegment(sketch, "E232.MirrorCS", {"start": v(340, -340) * mm, "end": v(260, -340) * mm, "construction": true});
            skLineSegment(sketch, "E233.MirrorCS", {"start": v(-340, -340) * mm, "end": v(-260, -340) * mm, "construction": true});
            skLineSegment(sketch, "E234.MirrorCS", {"start": v(340, -260) * mm, "end": v(340, -340) * mm, "construction": true});
            skLineSegment(sketch, "E235.MirrorCS", {"start": v(350, -350) * mm, "end": v(250, -250) * mm, "construction": true});
            skLineSegment(sketch, "E236.MirrorCS", {"start": v(260, -260) * mm, "end": v(260, -340) * mm, "construction": true});
            skLineSegment(sketch, "E237.MirrorCS", {"start": v(-260, -260) * mm, "end": v(-260, -340) * mm, "construction": true});
            skLineSegment(sketch, "E238.MirrorCS", {"start": v(-350, -350) * mm, "end": v(-250, -250) * mm, "construction": true});
            skLineSegment(sketch, "E239.MirrorCS", {"start": v(-340, -260) * mm, "end": v(-340, -340) * mm, "construction": true});
            skPoint(sketch, "E240.MirrorP", {"position": v(300, -300) * mm});
            skPoint(sketch, "E241.MirrorP", {"position": v(-300, -300) * mm});
            skLineSegment(sketch, "E242.MirrorCS", {"start": v(250, -350) * mm, "end": v(350, -250) * mm, "construction": true});
            skLineSegment(sketch, "E243.MirrorCS", {"start": v(-250, -350) * mm, "end": v(-350, -250) * mm, "construction": true});
            skLineSegment(sketch, "E244.MirrorCS", {"start": v(340, -260) * mm, "end": v(260, -260) * mm, "construction": true});
            skLineSegment(sketch, "E245.MirrorCS", {"start": v(-340, -260) * mm, "end": v(-260, -260) * mm, "construction": true});
            skSolve(sketch);
        }
        {
            var Q0;
            Q0=qSketchRegion(id+"F25",true);
            extrude(context, id + "F26", {"entities" : qUnion([Q0]), "depth" : 25 * mm});
        }
        {
            var Q0;
            Q0=makeQuery(id+"F25.imprint","IMPRINT",FACE,{"disambiguationData":[TD([[makeQuery(id+"F25.imprint","IMPRINT",EDGE,{"derivedFrom":sQuery(id+"F25.wireOp",EDGE,"E169")}),1.0]])]});
            var Q1;
            Q1=makeQuery(id+"F25.imprint","IMPRINT",FACE,{"disambiguationData":[TD([[makeQuery(id+"F25.imprint","IMPRINT",EDGE,{"derivedFrom":sQuery(id+"F25.wireOp",EDGE,"E170")}),1.0]])]});
            var Q2;
            Q2=makeQuery(id+"F25.imprint","IMPRINT",FACE,{"disambiguationData":[TD([[makeQuery(id+"F25.imprint","IMPRINT",EDGE,{"derivedFrom":sQuery(id+"F25.wireOp",EDGE,"E172")}),1.0]])]});
            var Q3;
            Q3=makeQuery(id+"F25.imprint","IMPRINT",FACE,{"disambiguationData":[TD([[makeQuery(id+"F25.imprint","IMPRINT",EDGE,{"derivedFrom":sQuery(id+"F25.wireOp",EDGE,"E171")}),1.0]])]});
            var Q4;
            Q4=makeQuery(id+"F25.imprint","IMPRINT",FACE,{"disambiguationData":[TD([[makeQuery(id+"F25.imprint","IMPRINT",EDGE,{"derivedFrom":sQuery(id+"F25.wireOp",EDGE,"E176.MirrorC")}),-1.0]])]});
            var Q5;
            Q5=makeQuery(id+"F25.imprint","IMPRINT",FACE,{"disambiguationData":[TD([[makeQuery(id+"F25.imprint","IMPRINT",EDGE,{"derivedFrom":sQuery(id+"F25.wireOp",EDGE,"E175.MirrorC")}),-1.0]])]});
            var Q6;
            Q6=makeQuery(id+"F25.imprint","IMPRINT",FACE,{"disambiguationData":[TD([[makeQuery(id+"F25.imprint","IMPRINT",EDGE,{"derivedFrom":sQuery(id+"F25.wireOp",EDGE,"E174.MirrorC")}),-1.0]])]});
            var Q7;
            Q7=makeQuery(id+"F25.imprint","IMPRINT",FACE,{"disambiguationData":[TD([[makeQuery(id+"F25.imprint","IMPRINT",EDGE,{"derivedFrom":sQuery(id+"F25.wireOp",EDGE,"E173.MirrorC")}),-1.0]])]});
            var Q8;
            Q8=makeQuery(id+"F25.imprint","IMPRINT",FACE,{"disambiguationData":[TD([[makeQuery(id+"F25.imprint","IMPRINT",EDGE,{"derivedFrom":sQuery(id+"F25.wireOp",EDGE,"E231.MirrorC")}),-1.0]])]});
            var Q9;
            Q9=makeQuery(id+"F25.imprint","IMPRINT",FACE,{"disambiguationData":[TD([[makeQuery(id+"F25.imprint","IMPRINT",EDGE,{"derivedFrom":sQuery(id+"F25.wireOp",EDGE,"E230.MirrorC")}),-1.0]])]});
            var Q10;
            Q10=makeQuery(id+"F25.imprint","IMPRINT",FACE,{"disambiguationData":[TD([[makeQuery(id+"F25.imprint","IMPRINT",EDGE,{"derivedFrom":sQuery(id+"F25.wireOp",EDGE,"E227.MirrorC")}),-1.0]])]});
            var Q11;
            Q11=makeQuery(id+"F25.imprint","IMPRINT",FACE,{"disambiguationData":[TD([[makeQuery(id+"F25.imprint","IMPRINT",EDGE,{"derivedFrom":sQuery(id+"F25.wireOp",EDGE,"E226.MirrorC")}),-1.0]])]});
            var Q12;
            Q12=makeQuery(id+"F25.imprint","IMPRINT",FACE,{"disambiguationData":[TD([[makeQuery(id+"F25.imprint","IMPRINT",EDGE,{"derivedFrom":sQuery(id+"F25.wireOp",EDGE,"E209")}),1.0]])]});
            var Q13;
            Q13=makeQuery(id+"F25.imprint","IMPRINT",FACE,{"disambiguationData":[TD([[makeQuery(id+"F25.imprint","IMPRINT",EDGE,{"derivedFrom":sQuery(id+"F25.wireOp",EDGE,"E210")}),1.0]])]});
            var Q14;
            Q14=makeQuery(id+"F25.imprint","IMPRINT",FACE,{"disambiguationData":[TD([[makeQuery(id+"F25.imprint","IMPRINT",EDGE,{"derivedFrom":sQuery(id+"F25.wireOp",EDGE,"E211")}),1.0]])]});
            var Q15;
            Q15=makeQuery(id+"F25.imprint","IMPRINT",FACE,{"disambiguationData":[TD([[makeQuery(id+"F25.imprint","IMPRINT",EDGE,{"derivedFrom":sQuery(id+"F25.wireOp",EDGE,"E212")}),1.0]])]});
            var Q16;
            Q16=makeQuery(id+"F25.imprint","IMPRINT",FACE,{"disambiguationData":[TD([[makeQuery(id+"F25.imprint","IMPRINT",EDGE,{"derivedFrom":sQuery(id+"F25.wireOp",EDGE,"E213.MirrorC")}),-1.0]])]});
            var Q17;
            Q17=makeQuery(id+"F25.imprint","IMPRINT",FACE,{"disambiguationData":[TD([[makeQuery(id+"F25.imprint","IMPRINT",EDGE,{"derivedFrom":sQuery(id+"F25.wireOp",EDGE,"E214.MirrorC")}),-1.0]])]});
            var Q18;
            Q18=makeQuery(id+"F25.imprint","IMPRINT",FACE,{"disambiguationData":[TD([[makeQuery(id+"F25.imprint","IMPRINT",EDGE,{"derivedFrom":sQuery(id+"F25.wireOp",EDGE,"E215.MirrorC")}),-1.0]])]});
            var Q19;
            Q19=makeQuery(id+"F25.imprint","IMPRINT",FACE,{"disambiguationData":[TD([[makeQuery(id+"F25.imprint","IMPRINT",EDGE,{"derivedFrom":sQuery(id+"F25.wireOp",EDGE,"E216.MirrorC")}),-1.0]])]});
            var Q20;
            Q20=makeQuery(id+"F25.imprint","IMPRINT",FACE,{"disambiguationData":[TD([[makeQuery(id+"F25.imprint","IMPRINT",EDGE,{"derivedFrom":sQuery(id+"F25.wireOp",EDGE,"E184.MirrorC")}),-1.0]])]});
            var Q21;
            Q21=makeQuery(id+"F25.imprint","IMPRINT",FACE,{"disambiguationData":[TD([[makeQuery(id+"F25.imprint","IMPRINT",EDGE,{"derivedFrom":sQuery(id+"F25.wireOp",EDGE,"E185.MirrorC")}),-1.0]])]});
            var Q22;
            Q22=makeQuery(id+"F25.imprint","IMPRINT",FACE,{"disambiguationData":[TD([[makeQuery(id+"F25.imprint","IMPRINT",EDGE,{"derivedFrom":sQuery(id+"F25.wireOp",EDGE,"E187.MirrorC")}),-1.0]])]});
            var Q23;
            Q23=makeQuery(id+"F25.imprint","IMPRINT",FACE,{"disambiguationData":[TD([[makeQuery(id+"F25.imprint","IMPRINT",EDGE,{"derivedFrom":sQuery(id+"F25.wireOp",EDGE,"E186.MirrorC")}),-1.0]])]});
            var Q24;
            Q24=makeQuery(id+"F25.imprint","IMPRINT",FACE,{"disambiguationData":[TD([[makeQuery(id+"F25.imprint","IMPRINT",EDGE,{"derivedFrom":sQuery(id+"F25.wireOp",EDGE,"E189.MirrorC")}),1.0]])]});
            var Q25;
            Q25=makeQuery(id+"F25.imprint","IMPRINT",FACE,{"disambiguationData":[TD([[makeQuery(id+"F25.imprint","IMPRINT",EDGE,{"derivedFrom":sQuery(id+"F25.wireOp",EDGE,"E188.MirrorC")}),1.0]])]});
            var Q26;
            Q26=makeQuery(id+"F25.imprint","IMPRINT",FACE,{"disambiguationData":[TD([[makeQuery(id+"F25.imprint","IMPRINT",EDGE,{"derivedFrom":sQuery(id+"F25.wireOp",EDGE,"E190.MirrorC")}),1.0]])]});
            var Q27;
            Q27=makeQuery(id+"F25.imprint","IMPRINT",FACE,{"disambiguationData":[TD([[makeQuery(id+"F25.imprint","IMPRINT",EDGE,{"derivedFrom":sQuery(id+"F25.wireOp",EDGE,"E191.MirrorC")}),1.0]])]});
            var Q28;
            Q28=makeQuery(id+"F25.imprint","IMPRINT",FACE,{"disambiguationData":[TD([[makeQuery(id+"F25.imprint","IMPRINT",EDGE,{"derivedFrom":sQuery(id+"F25.wireOp",EDGE,"E228.MirrorC")}),1.0]])]});
            var Q29;
            Q29=makeQuery(id+"F25.imprint","IMPRINT",FACE,{"disambiguationData":[TD([[makeQuery(id+"F25.imprint","IMPRINT",EDGE,{"derivedFrom":sQuery(id+"F25.wireOp",EDGE,"E229.MirrorC")}),1.0]])]});
            var Q30;
            Q30=makeQuery(id+"F25.imprint","IMPRINT",FACE,{"disambiguationData":[TD([[makeQuery(id+"F25.imprint","IMPRINT",EDGE,{"derivedFrom":sQuery(id+"F25.wireOp",EDGE,"E225.MirrorC")}),1.0]])]});
            var Q31;
            Q31=makeQuery(id+"F25.imprint","IMPRINT",FACE,{"disambiguationData":[TD([[makeQuery(id+"F25.imprint","IMPRINT",EDGE,{"derivedFrom":sQuery(id+"F25.wireOp",EDGE,"E224.MirrorC")}),1.0]])]});
            extrude(context, id + "F27", {"entities" : qUnion([Q0, Q1, Q2, Q3, Q4, Q5, Q6, Q7, Q8, Q9, Q10, Q11, Q12, Q13, Q14, Q15, Q16, Q17, Q18, Q19, Q20, Q21, Q22, Q23, Q24, Q25, Q26, Q27, Q28, Q29, Q30, Q31]), "operationType" : NewBodyOperationType.REMOVE, "oppositeDirection" : true, "depth" : 15 * mm});
        }
        {
            var Q0;
            Q0=makeQuery(id+"F26.opExtrude","CAP_FACE",FACE,{"disambiguationData":[OSD([sQuery(id+"F25.wireOp",EDGE,"E226.MirrorC"),sQuery(id+"F25.wireOp",EDGE,"E227.MirrorC"),sQuery(id+"F25.wireOp",EDGE,"E230.MirrorC"),sQuery(id+"F25.wireOp",EDGE,"E231.MirrorC"),sQuery(id+"F25.wireOp",EDGE,"E141.top"),sQuery(id+"F25.wireOp",EDGE,"E141.right"),sQuery(id+"F25.wireOp",EDGE,"E141.left"),sQuery(id+"F25.wireOp",EDGE,"E141.bottom")])],"isStart":false});
            var sketch = newSketch(context, id + "F28", { "sketchPlane" : qUnion([Q0])});
            skLineSegment(sketch, "E246.rect.bottom", {"start": v(-325, -350) * mm, "end": v(-275, -350) * mm});
            skLineSegment(sketch, "E246.rect.top", {"start": v(-325, -250) * mm, "end": v(-275, -250) * mm});
            skLineSegment(sketch, "E246.rect.left", {"start": v(-325, -350) * mm, "end": v(-325, -250) * mm});
            skLineSegment(sketch, "E246.rect.right", {"start": v(-275, -350) * mm, "end": v(-275, -250) * mm});
            skPoint(sketch, "E246.rect.middle", {"position": v(-300, -300) * mm});
            skLineSegment(sketch, "E247.rect.bottom", {"start": v(-650, -165) * mm, "end": v(-550, -165) * mm});
            skLineSegment(sketch, "E247.rect.top", {"start": v(-650, -115) * mm, "end": v(-550, -115) * mm});
            skLineSegment(sketch, "E247.rect.left", {"start": v(-650, -165) * mm, "end": v(-650, -115) * mm});
            skLineSegment(sketch, "E247.rect.right", {"start": v(-550, -165) * mm, "end": v(-550, -115) * mm});
            skPoint(sketch, "E247.rect.middle", {"position": v(-600, -140) * mm});
            skLineSegment(sketch, "E248.MirrorCS", {"start": v(-650, 115) * mm, "end": v(-550, 115) * mm});
            skLineSegment(sketch, "E249.MirrorCS", {"start": v(-550, 165) * mm, "end": v(-550, 115) * mm});
            skLineSegment(sketch, "E250.MirrorCS", {"start": v(-650, 165) * mm, "end": v(-650, 115) * mm});
            skPoint(sketch, "E251.MirrorP", {"position": v(-600, 140) * mm});
            skLineSegment(sketch, "E252.MirrorCS", {"start": v(-650, 165) * mm, "end": v(-550, 165) * mm});
            skLineSegment(sketch, "E253.MirrorCS", {"start": v(650, 165) * mm, "end": v(550, 165) * mm});
            skLineSegment(sketch, "E254.MirrorCS", {"start": v(550, 165) * mm, "end": v(550, 115) * mm});
            skLineSegment(sketch, "E255.MirrorCS", {"start": v(650, 165) * mm, "end": v(650, 115) * mm});
            skPoint(sketch, "E256.MirrorP", {"position": v(600, 140) * mm});
            skLineSegment(sketch, "E257.MirrorCS", {"start": v(650, 115) * mm, "end": v(550, 115) * mm});
            skLineSegment(sketch, "E258.MirrorCS", {"start": v(650, -115) * mm, "end": v(550, -115) * mm});
            skLineSegment(sketch, "E259.MirrorCS", {"start": v(550, -165) * mm, "end": v(550, -115) * mm});
            skLineSegment(sketch, "E260.MirrorCS", {"start": v(650, -165) * mm, "end": v(650, -115) * mm});
            skPoint(sketch, "E261.MirrorP", {"position": v(600, -140) * mm});
            skLineSegment(sketch, "E262.MirrorCS", {"start": v(650, -165) * mm, "end": v(550, -165) * mm});
            skLineSegment(sketch, "E263.MirrorCS", {"start": v(325, -250) * mm, "end": v(275, -250) * mm});
            skLineSegment(sketch, "E264.MirrorCS", {"start": v(275, -350) * mm, "end": v(275, -250) * mm});
            skLineSegment(sketch, "E265.MirrorCS", {"start": v(325, -350) * mm, "end": v(325, -250) * mm});
            skPoint(sketch, "E266.MirrorP", {"position": v(300, -300) * mm});
            skLineSegment(sketch, "E267.MirrorCS", {"start": v(325, -350) * mm, "end": v(275, -350) * mm});
            skLineSegment(sketch, "E268.MirrorCS", {"start": v(325, 250) * mm, "end": v(275, 250) * mm});
            skLineSegment(sketch, "E269.MirrorCS", {"start": v(-325, 250) * mm, "end": v(-275, 250) * mm});
            skLineSegment(sketch, "E270.MirrorCS", {"start": v(325, 350) * mm, "end": v(325, 250) * mm});
            skLineSegment(sketch, "E271.MirrorCS", {"start": v(275, 350) * mm, "end": v(275, 250) * mm});
            skLineSegment(sketch, "E272.MirrorCS", {"start": v(-275, 350) * mm, "end": v(-275, 250) * mm});
            skLineSegment(sketch, "E273.MirrorCS", {"start": v(-325, 350) * mm, "end": v(-325, 250) * mm});
            skPoint(sketch, "E274.MirrorP", {"position": v(300, 300) * mm});
            skPoint(sketch, "E275.MirrorP", {"position": v(-300, 300) * mm});
            skLineSegment(sketch, "E276.MirrorCS", {"start": v(325, 350) * mm, "end": v(275, 350) * mm});
            skLineSegment(sketch, "E277.MirrorCS", {"start": v(-325, 350) * mm, "end": v(-275, 350) * mm});
            skSolve(sketch);
        }
        {
            var Q0;
            Q0=qSketchRegion(id+"F28",true);
            extrude(context, id + "F29", {"entities" : qUnion([Q0]), "operationType" : NewBodyOperationType.ADD, "depth" : 100 * mm});
        }
        {
            var Q0;
            Q0=makeQuery(id+"F29.opExtrude","CAP_FACE",FACE,{"disambiguationData":[OSD([sQuery(id+"F28.wireOp",EDGE,"E246.rect.bottom"),sQuery(id+"F28.wireOp",EDGE,"E246.rect.top"),sQuery(id+"F28.wireOp",EDGE,"E246.rect.left"),sQuery(id+"F28.wireOp",EDGE,"E246.rect.right")])],"isStart":false});
            var sketch = newSketch(context, id + "F30", { "sketchPlane" : qUnion([Q0])});
            skLineSegment(sketch, "E278.bottom", {"start": v(-325, -250) * mm, "end": v(-275, -250) * mm});
            skLineSegment(sketch, "E278.top", {"start": v(-325, -350) * mm, "end": v(-275, -350) * mm});
            skLineSegment(sketch, "E278.left", {"start": v(-325, -250) * mm, "end": v(-325, -350) * mm});
            skLineSegment(sketch, "E278.right", {"start": v(-275, -250) * mm, "end": v(-275, -350) * mm});
            skLineSegment(sketch, "E279", {"start": v(-275, -250) * mm, "end": v(-325, -350) * mm, "construction": true});
            skLineSegment(sketch, "E280", {"start": v(-325, -250) * mm, "end": v(-275, -350) * mm, "construction": true});
            skLineSegment(sketch, "E281.rect.bottom", {"start": v(-317.5, -260) * mm, "end": v(-282.5, -260) * mm, "construction": true});
            skLineSegment(sketch, "E281.rect.top", {"start": v(-317.5, -340) * mm, "end": v(-282.5, -340) * mm, "construction": true});
            skLineSegment(sketch, "E281.rect.left", {"start": v(-317.5, -260) * mm, "end": v(-317.5, -340) * mm, "construction": true});
            skLineSegment(sketch, "E281.rect.right", {"start": v(-282.5, -260) * mm, "end": v(-282.5, -340) * mm, "construction": true});
            skPoint(sketch, "E281.rect.middle", {"position": v(-300, -300) * mm});
            skCircle(sketch, "E282", {"center": v(-317.5, -260) * mm, "radius": 3 * mm});
            skCircle(sketch, "E283", {"center": v(-282.5, -260) * mm, "radius": 3 * mm});
            skCircle(sketch, "E284", {"center": v(-317.5, -340) * mm, "radius": 3 * mm});
            skCircle(sketch, "E285", {"center": v(-282.5, -340) * mm, "radius": 3 * mm});
            skCircle(sketch, "E286.MirrorC", {"center": v(282.5, -260) * mm, "radius": 3 * mm});
            skCircle(sketch, "E287.MirrorC", {"center": v(317.5, -260) * mm, "radius": 3 * mm});
            skCircle(sketch, "E288.MirrorC", {"center": v(282.5, -340) * mm, "radius": 3 * mm});
            skCircle(sketch, "E289.MirrorC", {"center": v(317.5, -340) * mm, "radius": 3 * mm});
            skLineSegment(sketch, "E290.MirrorCS", {"start": v(325, -250) * mm, "end": v(275, -250) * mm});
            skLineSegment(sketch, "E291.MirrorCS", {"start": v(317.5, -260) * mm, "end": v(282.5, -260) * mm, "construction": true});
            skPoint(sketch, "E292.MirrorP", {"position": v(300, -300) * mm});
            skLineSegment(sketch, "E293.MirrorCS", {"start": v(275, -250) * mm, "end": v(275, -350) * mm});
            skLineSegment(sketch, "E294.MirrorCS", {"start": v(282.5, -260) * mm, "end": v(282.5, -340) * mm, "construction": true});
            skLineSegment(sketch, "E295.MirrorCS", {"start": v(325, -250) * mm, "end": v(275, -350) * mm, "construction": true});
            skLineSegment(sketch, "E296.MirrorCS", {"start": v(275, -250) * mm, "end": v(325, -350) * mm, "construction": true});
            skLineSegment(sketch, "E297.MirrorCS", {"start": v(317.5, -260) * mm, "end": v(317.5, -340) * mm, "construction": true});
            skLineSegment(sketch, "E298.MirrorCS", {"start": v(325, -250) * mm, "end": v(325, -350) * mm});
            skLineSegment(sketch, "E299.MirrorCS", {"start": v(317.5, -340) * mm, "end": v(282.5, -340) * mm, "construction": true});
            skLineSegment(sketch, "E300.MirrorCS", {"start": v(325, -350) * mm, "end": v(275, -350) * mm});
            skCircle(sketch, "E301.MirrorC", {"center": v(317.5, 260) * mm, "radius": 3 * mm});
            skCircle(sketch, "E302.MirrorC", {"center": v(282.5, 260) * mm, "radius": 3 * mm});
            skCircle(sketch, "E303.MirrorC", {"center": v(-282.5, 260) * mm, "radius": 3 * mm});
            skCircle(sketch, "E304.MirrorC", {"center": v(-317.5, 260) * mm, "radius": 3 * mm});
            skCircle(sketch, "E305.MirrorC", {"center": v(317.5, 340) * mm, "radius": 3 * mm});
            skCircle(sketch, "E306.MirrorC", {"center": v(282.5, 340) * mm, "radius": 3 * mm});
            skCircle(sketch, "E307.MirrorC", {"center": v(-282.5, 340) * mm, "radius": 3 * mm});
            skCircle(sketch, "E308.MirrorC", {"center": v(-317.5, 340) * mm, "radius": 3 * mm});
            skLineSegment(sketch, "E309.MirrorCS", {"start": v(-325, 250) * mm, "end": v(-275, 250) * mm});
            skLineSegment(sketch, "E310.MirrorCS", {"start": v(325, 250) * mm, "end": v(275, 250) * mm});
            skLineSegment(sketch, "E311.MirrorCS", {"start": v(317.5, 260) * mm, "end": v(282.5, 260) * mm, "construction": true});
            skLineSegment(sketch, "E312.MirrorCS", {"start": v(-317.5, 260) * mm, "end": v(-282.5, 260) * mm, "construction": true});
            skPoint(sketch, "E313.MirrorP", {"position": v(300, 300) * mm});
            skPoint(sketch, "E314.MirrorP", {"position": v(-300, 300) * mm});
            skLineSegment(sketch, "E315.MirrorCS", {"start": v(325, 250) * mm, "end": v(325, 350) * mm});
            skLineSegment(sketch, "E316.MirrorCS", {"start": v(317.5, 260) * mm, "end": v(317.5, 340) * mm, "construction": true});
            skLineSegment(sketch, "E317.MirrorCS", {"start": v(275, 250) * mm, "end": v(325, 350) * mm, "construction": true});
            skLineSegment(sketch, "E318.MirrorCS", {"start": v(325, 250) * mm, "end": v(275, 350) * mm, "construction": true});
            skLineSegment(sketch, "E319.MirrorCS", {"start": v(282.5, 260) * mm, "end": v(282.5, 340) * mm, "construction": true});
            skLineSegment(sketch, "E320.MirrorCS", {"start": v(275, 250) * mm, "end": v(275, 350) * mm});
            skLineSegment(sketch, "E321.MirrorCS", {"start": v(-275, 250) * mm, "end": v(-275, 350) * mm});
            skLineSegment(sketch, "E322.MirrorCS", {"start": v(-282.5, 260) * mm, "end": v(-282.5, 340) * mm, "construction": true});
            skLineSegment(sketch, "E323.MirrorCS", {"start": v(-325, 250) * mm, "end": v(-275, 350) * mm, "construction": true});
            skLineSegment(sketch, "E324.MirrorCS", {"start": v(-275, 250) * mm, "end": v(-325, 350) * mm, "construction": true});
            skLineSegment(sketch, "E325.MirrorCS", {"start": v(-317.5, 260) * mm, "end": v(-317.5, 340) * mm, "construction": true});
            skLineSegment(sketch, "E326.MirrorCS", {"start": v(-325, 250) * mm, "end": v(-325, 350) * mm});
            skLineSegment(sketch, "E327.MirrorCS", {"start": v(317.5, 340) * mm, "end": v(282.5, 340) * mm, "construction": true});
            skLineSegment(sketch, "E328.MirrorCS", {"start": v(-317.5, 340) * mm, "end": v(-282.5, 340) * mm, "construction": true});
            skLineSegment(sketch, "E329.MirrorCS", {"start": v(325, 350) * mm, "end": v(275, 350) * mm});
            skLineSegment(sketch, "E330.MirrorCS", {"start": v(-325, 350) * mm, "end": v(-275, 350) * mm});
            skLineSegment(sketch, "E331.bottom", {"start": v(-650, -115) * mm, "end": v(-550, -115) * mm});
            skLineSegment(sketch, "E331.top", {"start": v(-650, -165) * mm, "end": v(-550, -165) * mm});
            skLineSegment(sketch, "E331.left", {"start": v(-650, -115) * mm, "end": v(-650, -165) * mm});
            skLineSegment(sketch, "E331.right", {"start": v(-550, -115) * mm, "end": v(-550, -165) * mm});
            skLineSegment(sketch, "E332", {"start": v(-650, -115) * mm, "end": v(-550, -165) * mm, "construction": true});
            skLineSegment(sketch, "E333", {"start": v(-550, -115) * mm, "end": v(-650, -165) * mm, "construction": true});
            skLineSegment(sketch, "E334.rect.bottom", {"start": v(-640, -157.5) * mm, "end": v(-560, -157.5) * mm, "construction": true});
            skLineSegment(sketch, "E334.rect.top", {"start": v(-640, -122.5) * mm, "end": v(-560, -122.5) * mm, "construction": true});
            skLineSegment(sketch, "E334.rect.left", {"start": v(-640, -157.5) * mm, "end": v(-640, -122.5) * mm, "construction": true});
            skLineSegment(sketch, "E334.rect.right", {"start": v(-560, -157.5) * mm, "end": v(-560, -122.5) * mm, "construction": true});
            skPoint(sketch, "E334.rect.middle", {"position": v(-600, -140) * mm});
            skCircle(sketch, "E335", {"center": v(-640, -122.5) * mm, "radius": 3 * mm});
            skCircle(sketch, "E336", {"center": v(-560, -122.5) * mm, "radius": 3 * mm});
            skCircle(sketch, "E337", {"center": v(-640, -157.5) * mm, "radius": 3 * mm});
            skCircle(sketch, "E338", {"center": v(-560, -157.5) * mm, "radius": 3 * mm});
            skCircle(sketch, "E339.MirrorC", {"center": v(-560, 122.5) * mm, "radius": 3 * mm});
            skCircle(sketch, "E340.MirrorC", {"center": v(-640, 122.5) * mm, "radius": 3 * mm});
            skCircle(sketch, "E341.MirrorC", {"center": v(-560, 157.5) * mm, "radius": 3 * mm});
            skCircle(sketch, "E342.MirrorC", {"center": v(-640, 157.5) * mm, "radius": 3 * mm});
            skLineSegment(sketch, "E343.MirrorCS", {"start": v(-650, 115) * mm, "end": v(-550, 115) * mm});
            skLineSegment(sketch, "E344.MirrorCS", {"start": v(-550, 115) * mm, "end": v(-550, 165) * mm});
            skLineSegment(sketch, "E345.MirrorCS", {"start": v(-640, 122.5) * mm, "end": v(-560, 122.5) * mm, "construction": true});
            skLineSegment(sketch, "E346.MirrorCS", {"start": v(-560, 157.5) * mm, "end": v(-560, 122.5) * mm, "construction": true});
            skLineSegment(sketch, "E347.MirrorCS", {"start": v(-640, 157.5) * mm, "end": v(-640, 122.5) * mm, "construction": true});
            skLineSegment(sketch, "E348.MirrorCS", {"start": v(-650, 115) * mm, "end": v(-550, 165) * mm, "construction": true});
            skPoint(sketch, "E349.MirrorP", {"position": v(-600, 140) * mm});
            skLineSegment(sketch, "E350.MirrorCS", {"start": v(-550, 115) * mm, "end": v(-650, 165) * mm, "construction": true});
            skLineSegment(sketch, "E351.MirrorCS", {"start": v(-650, 115) * mm, "end": v(-650, 165) * mm});
            skLineSegment(sketch, "E352.MirrorCS", {"start": v(-640, 157.5) * mm, "end": v(-560, 157.5) * mm, "construction": true});
            skLineSegment(sketch, "E353.MirrorCS", {"start": v(-650, 165) * mm, "end": v(-550, 165) * mm});
            skCircle(sketch, "E354.MirrorC", {"center": v(560, 157.5) * mm, "radius": 3 * mm});
            skCircle(sketch, "E355.MirrorC", {"center": v(640, 157.5) * mm, "radius": 3 * mm});
            skCircle(sketch, "E356.MirrorC", {"center": v(560, 122.5) * mm, "radius": 3 * mm});
            skCircle(sketch, "E357.MirrorC", {"center": v(640, 122.5) * mm, "radius": 3 * mm});
            skCircle(sketch, "E358.MirrorC", {"center": v(560, -122.5) * mm, "radius": 3 * mm});
            skCircle(sketch, "E359.MirrorC", {"center": v(640, -122.5) * mm, "radius": 3 * mm});
            skCircle(sketch, "E360.MirrorC", {"center": v(560, -157.5) * mm, "radius": 3 * mm});
            skCircle(sketch, "E361.MirrorC", {"center": v(640, -157.5) * mm, "radius": 3 * mm});
            skLineSegment(sketch, "E362.MirrorCS", {"start": v(650, 165) * mm, "end": v(550, 165) * mm});
            skLineSegment(sketch, "E363.MirrorCS", {"start": v(640, 157.5) * mm, "end": v(560, 157.5) * mm, "construction": true});
            skLineSegment(sketch, "E364.MirrorCS", {"start": v(560, 157.5) * mm, "end": v(560, 122.5) * mm, "construction": true});
            skLineSegment(sketch, "E365.MirrorCS", {"start": v(640, 157.5) * mm, "end": v(640, 122.5) * mm, "construction": true});
            skPoint(sketch, "E366.MirrorP", {"position": v(600, 140) * mm});
            skLineSegment(sketch, "E367.MirrorCS", {"start": v(550, 115) * mm, "end": v(550, 165) * mm});
            skLineSegment(sketch, "E368.MirrorCS", {"start": v(650, 115) * mm, "end": v(550, 165) * mm, "construction": true});
            skLineSegment(sketch, "E369.MirrorCS", {"start": v(650, 115) * mm, "end": v(650, 165) * mm});
            skLineSegment(sketch, "E370.MirrorCS", {"start": v(550, 115) * mm, "end": v(650, 165) * mm, "construction": true});
            skLineSegment(sketch, "E371.MirrorCS", {"start": v(640, 122.5) * mm, "end": v(560, 122.5) * mm, "construction": true});
            skLineSegment(sketch, "E372.MirrorCS", {"start": v(650, 115) * mm, "end": v(550, 115) * mm});
            skLineSegment(sketch, "E373.MirrorCS", {"start": v(650, -115) * mm, "end": v(550, -115) * mm});
            skLineSegment(sketch, "E374.MirrorCS", {"start": v(640, -122.5) * mm, "end": v(560, -122.5) * mm, "construction": true});
            skLineSegment(sketch, "E375.MirrorCS", {"start": v(550, -115) * mm, "end": v(550, -165) * mm});
            skLineSegment(sketch, "E376.MirrorCS", {"start": v(560, -157.5) * mm, "end": v(560, -122.5) * mm, "construction": true});
            skLineSegment(sketch, "E377.MirrorCS", {"start": v(640, -157.5) * mm, "end": v(640, -122.5) * mm, "construction": true});
            skLineSegment(sketch, "E378.MirrorCS", {"start": v(650, -115) * mm, "end": v(550, -165) * mm, "construction": true});
            skPoint(sketch, "E379.MirrorP", {"position": v(600, -140) * mm});
            skLineSegment(sketch, "E380.MirrorCS", {"start": v(550, -115) * mm, "end": v(650, -165) * mm, "construction": true});
            skLineSegment(sketch, "E381.MirrorCS", {"start": v(650, -115) * mm, "end": v(650, -165) * mm});
            skLineSegment(sketch, "E382.MirrorCS", {"start": v(640, -157.5) * mm, "end": v(560, -157.5) * mm, "construction": true});
            skLineSegment(sketch, "E383.MirrorCS", {"start": v(650, -165) * mm, "end": v(550, -165) * mm});
            skSolve(sketch);
        }
        {
            var Q0;
            Q0=makeQuery(id+"F30.imprint","IMPRINT",FACE,{"disambiguationData":[TD([[makeQuery(id+"F30.imprint","IMPRINT",EDGE,{"derivedFrom":sQuery(id+"F30.wireOp",EDGE,"E284")}),1.0]])]});
            var Q1;
            Q1=makeQuery(id+"F30.imprint","IMPRINT",FACE,{"disambiguationData":[TD([[makeQuery(id+"F30.imprint","IMPRINT",EDGE,{"derivedFrom":sQuery(id+"F30.wireOp",EDGE,"E285")}),1.0]])]});
            var Q2;
            Q2=makeQuery(id+"F30.imprint","IMPRINT",FACE,{"disambiguationData":[TD([[makeQuery(id+"F30.imprint","IMPRINT",EDGE,{"derivedFrom":sQuery(id+"F30.wireOp",EDGE,"E283")}),1.0]])]});
            var Q3;
            Q3=makeQuery(id+"F30.imprint","IMPRINT",FACE,{"disambiguationData":[TD([[makeQuery(id+"F30.imprint","IMPRINT",EDGE,{"derivedFrom":sQuery(id+"F30.wireOp",EDGE,"E282")}),1.0]])]});
            var Q4;
            Q4=makeQuery(id+"F30.imprint","IMPRINT",FACE,{"disambiguationData":[TD([[makeQuery(id+"F30.imprint","IMPRINT",EDGE,{"derivedFrom":sQuery(id+"F30.wireOp",EDGE,"E337")}),1.0]])]});
            var Q5;
            Q5=makeQuery(id+"F30.imprint","IMPRINT",FACE,{"disambiguationData":[TD([[makeQuery(id+"F30.imprint","IMPRINT",EDGE,{"derivedFrom":sQuery(id+"F30.wireOp",EDGE,"E335")}),1.0]])]});
            var Q6;
            Q6=makeQuery(id+"F30.imprint","IMPRINT",FACE,{"disambiguationData":[TD([[makeQuery(id+"F30.imprint","IMPRINT",EDGE,{"derivedFrom":sQuery(id+"F30.wireOp",EDGE,"E338")}),1.0]])]});
            var Q7;
            Q7=makeQuery(id+"F30.imprint","IMPRINT",FACE,{"disambiguationData":[TD([[makeQuery(id+"F30.imprint","IMPRINT",EDGE,{"derivedFrom":sQuery(id+"F30.wireOp",EDGE,"E336")}),1.0]])]});
            var Q8;
            Q8=makeQuery(id+"F30.imprint","IMPRINT",FACE,{"disambiguationData":[TD([[makeQuery(id+"F30.imprint","IMPRINT",EDGE,{"derivedFrom":sQuery(id+"F30.wireOp",EDGE,"E340.MirrorC")}),-1.0]])]});
            var Q9;
            Q9=makeQuery(id+"F30.imprint","IMPRINT",FACE,{"disambiguationData":[TD([[makeQuery(id+"F30.imprint","IMPRINT",EDGE,{"derivedFrom":sQuery(id+"F30.wireOp",EDGE,"E342.MirrorC")}),-1.0]])]});
            var Q10;
            Q10=makeQuery(id+"F30.imprint","IMPRINT",FACE,{"disambiguationData":[TD([[makeQuery(id+"F30.imprint","IMPRINT",EDGE,{"derivedFrom":sQuery(id+"F30.wireOp",EDGE,"E339.MirrorC")}),-1.0]])]});
            var Q11;
            Q11=makeQuery(id+"F30.imprint","IMPRINT",FACE,{"disambiguationData":[TD([[makeQuery(id+"F30.imprint","IMPRINT",EDGE,{"derivedFrom":sQuery(id+"F30.wireOp",EDGE,"E341.MirrorC")}),-1.0]])]});
            var Q12;
            Q12=makeQuery(id+"F30.imprint","IMPRINT",FACE,{"disambiguationData":[TD([[makeQuery(id+"F30.imprint","IMPRINT",EDGE,{"derivedFrom":sQuery(id+"F30.wireOp",EDGE,"E304.MirrorC")}),-1.0]])]});
            var Q13;
            Q13=makeQuery(id+"F30.imprint","IMPRINT",FACE,{"disambiguationData":[TD([[makeQuery(id+"F30.imprint","IMPRINT",EDGE,{"derivedFrom":sQuery(id+"F30.wireOp",EDGE,"E303.MirrorC")}),-1.0]])]});
            var Q14;
            Q14=makeQuery(id+"F30.imprint","IMPRINT",FACE,{"disambiguationData":[TD([[makeQuery(id+"F30.imprint","IMPRINT",EDGE,{"derivedFrom":sQuery(id+"F30.wireOp",EDGE,"E307.MirrorC")}),-1.0]])]});
            var Q15;
            Q15=makeQuery(id+"F30.imprint","IMPRINT",FACE,{"disambiguationData":[TD([[makeQuery(id+"F30.imprint","IMPRINT",EDGE,{"derivedFrom":sQuery(id+"F30.wireOp",EDGE,"E308.MirrorC")}),-1.0]])]});
            var Q16;
            Q16=makeQuery(id+"F30.imprint","IMPRINT",FACE,{"disambiguationData":[TD([[makeQuery(id+"F30.imprint","IMPRINT",EDGE,{"derivedFrom":sQuery(id+"F30.wireOp",EDGE,"E288.MirrorC")}),-1.0]])]});
            var Q17;
            Q17=makeQuery(id+"F30.imprint","IMPRINT",FACE,{"disambiguationData":[TD([[makeQuery(id+"F30.imprint","IMPRINT",EDGE,{"derivedFrom":sQuery(id+"F30.wireOp",EDGE,"E286.MirrorC")}),-1.0]])]});
            var Q18;
            Q18=makeQuery(id+"F30.imprint","IMPRINT",FACE,{"disambiguationData":[TD([[makeQuery(id+"F30.imprint","IMPRINT",EDGE,{"derivedFrom":sQuery(id+"F30.wireOp",EDGE,"E287.MirrorC")}),-1.0]])]});
            var Q19;
            Q19=makeQuery(id+"F30.imprint","IMPRINT",FACE,{"disambiguationData":[TD([[makeQuery(id+"F30.imprint","IMPRINT",EDGE,{"derivedFrom":sQuery(id+"F30.wireOp",EDGE,"E289.MirrorC")}),-1.0]])]});
            var Q20;
            Q20=makeQuery(id+"F30.imprint","IMPRINT",FACE,{"disambiguationData":[TD([[makeQuery(id+"F30.imprint","IMPRINT",EDGE,{"derivedFrom":sQuery(id+"F30.wireOp",EDGE,"E302.MirrorC")}),1.0]])]});
            var Q21;
            Q21=makeQuery(id+"F30.imprint","IMPRINT",FACE,{"disambiguationData":[TD([[makeQuery(id+"F30.imprint","IMPRINT",EDGE,{"derivedFrom":sQuery(id+"F30.wireOp",EDGE,"E301.MirrorC")}),1.0]])]});
            var Q22;
            Q22=makeQuery(id+"F30.imprint","IMPRINT",FACE,{"disambiguationData":[TD([[makeQuery(id+"F30.imprint","IMPRINT",EDGE,{"derivedFrom":sQuery(id+"F30.wireOp",EDGE,"E306.MirrorC")}),1.0]])]});
            var Q23;
            Q23=makeQuery(id+"F30.imprint","IMPRINT",FACE,{"disambiguationData":[TD([[makeQuery(id+"F30.imprint","IMPRINT",EDGE,{"derivedFrom":sQuery(id+"F30.wireOp",EDGE,"E305.MirrorC")}),1.0]])]});
            var Q24;
            Q24=makeQuery(id+"F30.imprint","IMPRINT",FACE,{"disambiguationData":[TD([[makeQuery(id+"F30.imprint","IMPRINT",EDGE,{"derivedFrom":sQuery(id+"F30.wireOp",EDGE,"E360.MirrorC")}),-1.0]])]});
            var Q25;
            Q25=makeQuery(id+"F30.imprint","IMPRINT",FACE,{"disambiguationData":[TD([[makeQuery(id+"F30.imprint","IMPRINT",EDGE,{"derivedFrom":sQuery(id+"F30.wireOp",EDGE,"E358.MirrorC")}),-1.0]])]});
            var Q26;
            Q26=makeQuery(id+"F30.imprint","IMPRINT",FACE,{"disambiguationData":[TD([[makeQuery(id+"F30.imprint","IMPRINT",EDGE,{"derivedFrom":sQuery(id+"F30.wireOp",EDGE,"E361.MirrorC")}),-1.0]])]});
            var Q27;
            Q27=makeQuery(id+"F30.imprint","IMPRINT",FACE,{"disambiguationData":[TD([[makeQuery(id+"F30.imprint","IMPRINT",EDGE,{"derivedFrom":sQuery(id+"F30.wireOp",EDGE,"E359.MirrorC")}),-1.0]])]});
            var Q28;
            Q28=makeQuery(id+"F30.imprint","IMPRINT",FACE,{"disambiguationData":[TD([[makeQuery(id+"F30.imprint","IMPRINT",EDGE,{"derivedFrom":sQuery(id+"F30.wireOp",EDGE,"E356.MirrorC")}),1.0]])]});
            var Q29;
            Q29=makeQuery(id+"F30.imprint","IMPRINT",FACE,{"disambiguationData":[TD([[makeQuery(id+"F30.imprint","IMPRINT",EDGE,{"derivedFrom":sQuery(id+"F30.wireOp",EDGE,"E354.MirrorC")}),1.0]])]});
            var Q30;
            Q30=makeQuery(id+"F30.imprint","IMPRINT",FACE,{"disambiguationData":[TD([[makeQuery(id+"F30.imprint","IMPRINT",EDGE,{"derivedFrom":sQuery(id+"F30.wireOp",EDGE,"E355.MirrorC")}),1.0]])]});
            var Q31;
            Q31=makeQuery(id+"F30.imprint","IMPRINT",FACE,{"disambiguationData":[TD([[makeQuery(id+"F30.imprint","IMPRINT",EDGE,{"derivedFrom":sQuery(id+"F30.wireOp",EDGE,"E357.MirrorC")}),1.0]])]});
            extrude(context, id + "F31", {"entities" : qUnion([Q0, Q1, Q2, Q3, Q4, Q5, Q6, Q7, Q8, Q9, Q10, Q11, Q12, Q13, Q14, Q15, Q16, Q17, Q18, Q19, Q20, Q21, Q22, Q23, Q24, Q25, Q26, Q27, Q28, Q29, Q30, Q31]), "operationType" : NewBodyOperationType.REMOVE, "oppositeDirection" : true, "depth" : 25 * mm});
        }
        {
            var Q0;
            Q0=qSketchRegion(id+"F30",true);
            extrude(context, id + "F32", {"entities" : qUnion([Q0]), "depth" : 25 * mm});
        }
        {
            var Q0;
            Q0=makeQuery(id+"F32.opExtrude","CAP_FACE",FACE,{"disambiguationData":[OSD([sQuery(id+"F30.wireOp",EDGE,"E278.bottom"),sQuery(id+"F30.wireOp",EDGE,"E278.top"),sQuery(id+"F30.wireOp",EDGE,"E278.left"),sQuery(id+"F30.wireOp",EDGE,"E278.right"),sQuery(id+"F30.wireOp",EDGE,"E282"),sQuery(id+"F30.wireOp",EDGE,"E283"),sQuery(id+"F30.wireOp",EDGE,"E284"),sQuery(id+"F30.wireOp",EDGE,"E285")])],"isStart":false});
            var sketch = newSketch(context, id + "F33", { "sketchPlane" : qUnion([Q0])});
            skLineSegment(sketch, "E384.rect.bottom", {"start": v(-325, -273.85) * mm, "end": v(-275, -273.85) * mm});
            skLineSegment(sketch, "E384.rect.top", {"start": v(-325, -326.15) * mm, "end": v(-275, -326.15) * mm});
            skLineSegment(sketch, "E384.rect.left", {"start": v(-325, -273.85) * mm, "end": v(-325, -326.15) * mm});
            skLineSegment(sketch, "E384.rect.right", {"start": v(-275, -273.85) * mm, "end": v(-275, -326.15) * mm});
            skPoint(sketch, "E384.rect.middle", {"position": v(-300, -300) * mm});
            skLineSegment(sketch, "E385.rect.bottom", {"start": v(-325, -283.85) * mm, "end": v(-275, -283.85) * mm});
            skLineSegment(sketch, "E385.rect.top", {"start": v(-325, -316.15) * mm, "end": v(-275, -316.15) * mm});
            skLineSegment(sketch, "E385.rect.left", {"start": v(-325, -283.85) * mm, "end": v(-325, -316.15) * mm});
            skLineSegment(sketch, "E385.rect.right", {"start": v(-275, -283.85) * mm, "end": v(-275, -316.15) * mm});
            skLineSegment(sketch, "E386.MirrorCS", {"start": v(325, -273.85) * mm, "end": v(325, -326.15) * mm});
            skLineSegment(sketch, "E387.MirrorCS", {"start": v(325, -283.85) * mm, "end": v(325, -316.15) * mm});
            skLineSegment(sketch, "E388.MirrorCS", {"start": v(275, -273.85) * mm, "end": v(275, -326.15) * mm});
            skPoint(sketch, "E389.MirrorP", {"position": v(300, -300) * mm});
            skLineSegment(sketch, "E390.MirrorCS", {"start": v(325, -273.85) * mm, "end": v(275, -273.85) * mm});
            skLineSegment(sketch, "E391.MirrorCS", {"start": v(325, -283.85) * mm, "end": v(275, -283.85) * mm});
            skLineSegment(sketch, "E392.MirrorCS", {"start": v(275, -283.85) * mm, "end": v(275, -316.15) * mm});
            skLineSegment(sketch, "E393.MirrorCS", {"start": v(325, -316.15) * mm, "end": v(275, -316.15) * mm});
            skLineSegment(sketch, "E394.MirrorCS", {"start": v(325, -326.15) * mm, "end": v(275, -326.15) * mm});
            skLineSegment(sketch, "E395.MirrorCS", {"start": v(-325, 283.85) * mm, "end": v(-325, 316.15) * mm});
            skLineSegment(sketch, "E396.MirrorCS", {"start": v(325, 283.85) * mm, "end": v(325, 316.15) * mm});
            skLineSegment(sketch, "E397.MirrorCS", {"start": v(-275, 283.85) * mm, "end": v(-275, 316.15) * mm});
            skLineSegment(sketch, "E398.MirrorCS", {"start": v(-325, 273.85) * mm, "end": v(-325, 326.15) * mm});
            skLineSegment(sketch, "E399.MirrorCS", {"start": v(325, 283.85) * mm, "end": v(275, 283.85) * mm});
            skLineSegment(sketch, "E400.MirrorCS", {"start": v(-325, 283.85) * mm, "end": v(-275, 283.85) * mm});
            skLineSegment(sketch, "E401.MirrorCS", {"start": v(275, 283.85) * mm, "end": v(275, 316.15) * mm});
            skLineSegment(sketch, "E402.MirrorCS", {"start": v(325, 316.15) * mm, "end": v(275, 316.15) * mm});
            skLineSegment(sketch, "E403.MirrorCS", {"start": v(-325, 316.15) * mm, "end": v(-275, 316.15) * mm});
            skLineSegment(sketch, "E404.MirrorCS", {"start": v(325, 273.85) * mm, "end": v(325, 326.15) * mm});
            skLineSegment(sketch, "E405.MirrorCS", {"start": v(275, 273.85) * mm, "end": v(275, 326.15) * mm});
            skLineSegment(sketch, "E406.MirrorCS", {"start": v(-275, 273.85) * mm, "end": v(-275, 326.15) * mm});
            skLineSegment(sketch, "E407.MirrorCS", {"start": v(-325, 273.85) * mm, "end": v(-275, 273.85) * mm});
            skPoint(sketch, "E408.MirrorP", {"position": v(300, 300) * mm});
            skPoint(sketch, "E409.MirrorP", {"position": v(-300, 300) * mm});
            skLineSegment(sketch, "E410.MirrorCS", {"start": v(325, 273.85) * mm, "end": v(275, 273.85) * mm});
            skLineSegment(sketch, "E411.MirrorCS", {"start": v(325, 326.15) * mm, "end": v(275, 326.15) * mm});
            skLineSegment(sketch, "E412.MirrorCS", {"start": v(-325, 326.15) * mm, "end": v(-275, 326.15) * mm});
            skSolve(sketch);
        }
        {
            var Q0;
            Q0=makeQuery(id+"F33.imprint","IMPRINT",FACE,{"disambiguationData":[TD([[makeQuery(id+"F33.imprint","IMPRINT",EDGE,{"derivedFrom":sQuery(id+"F33.wireOp",EDGE,"E385.rect.bottom")}),-1.0]])]});
            var Q1;
            Q1=makeQuery(id+"F33.imprint","IMPRINT",FACE,{"disambiguationData":[TD([[makeQuery(id+"F33.imprint","IMPRINT",EDGE,{"derivedFrom":sQuery(id+"F33.wireOp",EDGE,"E387.MirrorCS")}),-1.0]])]});
            var Q2;
            {var subQ2=sQuery(id+"F33.wireOp",EDGE,"E400.MirrorCS");Q2=makeQuery(id+"F33.imprint","IMPRINT",FACE,{"disambiguationData":[TD([[makeQuery(id+"F33.imprint","IMPRINT",EDGE,{"derivedFrom":subQ2}),1.0]])]});}
            var Q3;
            {var subQ2=sQuery(id+"F33.wireOp",EDGE,"E399.MirrorCS");Q3=makeQuery(id+"F33.imprint","IMPRINT",FACE,{"disambiguationData":[TD([[makeQuery(id+"F33.imprint","IMPRINT",EDGE,{"derivedFrom":subQ2}),-1.0]])]});}
            extrude(context, id + "F34", {"entities" : qUnion([Q0, Q1, Q2, Q3]), "operationType" : NewBodyOperationType.ADD, "depth" : 25 * mm});
        }
        {
            var Q0;
            {var subQ2=sQuery(id+"F33.wireOp",EDGE,"E384.rect.bottom");Q0=makeQuery(id+"F33.imprint","IMPRINT",FACE,{"disambiguationData":[TD([[makeQuery(id+"F33.imprint","IMPRINT",EDGE,{"derivedFrom":subQ2}),-1.0]])]});}
            var Q1;
            {var subQ2=sQuery(id+"F33.wireOp",EDGE,"E384.rect.top");Q1=makeQuery(id+"F33.imprint","IMPRINT",FACE,{"disambiguationData":[TD([[makeQuery(id+"F33.imprint","IMPRINT",EDGE,{"derivedFrom":subQ2}),1.0]])]});}
            var Q2;
            {var subQ1=sQuery(id+"F33.wireOp",EDGE,"E390.MirrorCS");Q2=makeQuery(id+"F33.imprint","IMPRINT",FACE,{"disambiguationData":[TD([[makeQuery(id+"F33.imprint","IMPRINT",EDGE,{"derivedFrom":subQ1}),1.0]])]});}
            var Q3;
            {var subQ1=sQuery(id+"F33.wireOp",EDGE,"E393.MirrorCS");Q3=makeQuery(id+"F33.imprint","IMPRINT",FACE,{"disambiguationData":[TD([[makeQuery(id+"F33.imprint","IMPRINT",EDGE,{"derivedFrom":subQ1}),1.0]])]});}
            var Q4;
            {var subQ2=sQuery(id+"F33.wireOp",EDGE,"E400.MirrorCS");Q4=makeQuery(id+"F33.imprint","IMPRINT",FACE,{"disambiguationData":[TD([[makeQuery(id+"F33.imprint","IMPRINT",EDGE,{"derivedFrom":subQ2}),-1.0]])]});}
            var Q5;
            {var subQ1=sQuery(id+"F33.wireOp",EDGE,"E403.MirrorCS");Q5=makeQuery(id+"F33.imprint","IMPRINT",FACE,{"disambiguationData":[TD([[makeQuery(id+"F33.imprint","IMPRINT",EDGE,{"derivedFrom":subQ1}),1.0]])]});}
            var Q6;
            {var subQ2=sQuery(id+"F33.wireOp",EDGE,"E402.MirrorCS");Q6=makeQuery(id+"F33.imprint","IMPRINT",FACE,{"disambiguationData":[TD([[makeQuery(id+"F33.imprint","IMPRINT",EDGE,{"derivedFrom":subQ2}),-1.0]])]});}
            var Q7;
            {var subQ2=sQuery(id+"F33.wireOp",EDGE,"E399.MirrorCS");Q7=makeQuery(id+"F33.imprint","IMPRINT",FACE,{"disambiguationData":[TD([[makeQuery(id+"F33.imprint","IMPRINT",EDGE,{"derivedFrom":subQ2}),1.0]])]});}
            extrude(context, id + "F35", {"entities" : qUnion([Q0, Q1, Q2, Q3, Q4, Q5, Q6, Q7]), "operationType" : NewBodyOperationType.ADD, "depth" : 50 * mm});
        }
        {
            var Q0;
            Q0=makeQuery(id+"F32.opExtrude","CAP_FACE",FACE,{"disambiguationData":[OSD([sQuery(id+"F30.wireOp",EDGE,"E331.bottom"),sQuery(id+"F30.wireOp",EDGE,"E331.top"),sQuery(id+"F30.wireOp",EDGE,"E331.left"),sQuery(id+"F30.wireOp",EDGE,"E331.right"),sQuery(id+"F30.wireOp",EDGE,"E335"),sQuery(id+"F30.wireOp",EDGE,"E336"),sQuery(id+"F30.wireOp",EDGE,"E337"),sQuery(id+"F30.wireOp",EDGE,"E338")])],"isStart":false});
            var sketch = newSketch(context, id + "F36", { "sketchPlane" : qUnion([Q0])});
            skLineSegment(sketch, "E413.rect.bottom", {"start": v(-626.15, -115) * mm, "end": v(-573.85, -115) * mm});
            skLineSegment(sketch, "E413.rect.top", {"start": v(-626.15, -165) * mm, "end": v(-573.85, -165) * mm});
            skLineSegment(sketch, "E413.rect.left", {"start": v(-626.15, -115) * mm, "end": v(-626.15, -165) * mm});
            skLineSegment(sketch, "E413.rect.right", {"start": v(-573.85, -115) * mm, "end": v(-573.85, -165) * mm});
            skPoint(sketch, "E413.rect.middle", {"position": v(-600, -140) * mm});
            skLineSegment(sketch, "E414.rect.bottom", {"start": v(-616.15, -115) * mm, "end": v(-583.85, -115) * mm});
            skLineSegment(sketch, "E414.rect.top", {"start": v(-616.15, -165) * mm, "end": v(-583.85, -165) * mm});
            skLineSegment(sketch, "E414.rect.left", {"start": v(-616.15, -115) * mm, "end": v(-616.15, -165) * mm});
            skLineSegment(sketch, "E414.rect.right", {"start": v(-583.85, -115) * mm, "end": v(-583.85, -165) * mm});
            skLineSegment(sketch, "E415.MirrorCS", {"start": v(-616.15, 115) * mm, "end": v(-583.85, 115) * mm});
            skLineSegment(sketch, "E416.MirrorCS", {"start": v(-626.15, 115) * mm, "end": v(-573.85, 115) * mm});
            skPoint(sketch, "E417.MirrorP", {"position": v(-600, 140) * mm});
            skLineSegment(sketch, "E418.MirrorCS", {"start": v(-616.15, 165) * mm, "end": v(-583.85, 165) * mm});
            skLineSegment(sketch, "E419.MirrorCS", {"start": v(-573.85, 115) * mm, "end": v(-573.85, 165) * mm});
            skLineSegment(sketch, "E420.MirrorCS", {"start": v(-583.85, 115) * mm, "end": v(-583.85, 165) * mm});
            skLineSegment(sketch, "E421.MirrorCS", {"start": v(-616.15, 115) * mm, "end": v(-616.15, 165) * mm});
            skLineSegment(sketch, "E422.MirrorCS", {"start": v(-626.15, 115) * mm, "end": v(-626.15, 165) * mm});
            skLineSegment(sketch, "E423.MirrorCS", {"start": v(-626.15, 165) * mm, "end": v(-573.85, 165) * mm});
            skLineSegment(sketch, "E424.MirrorCS", {"start": v(616.15, -115) * mm, "end": v(583.85, -115) * mm});
            skLineSegment(sketch, "E425.MirrorCS", {"start": v(626.15, -115) * mm, "end": v(573.85, -115) * mm});
            skLineSegment(sketch, "E426.MirrorCS", {"start": v(616.15, 165) * mm, "end": v(583.85, 165) * mm});
            skLineSegment(sketch, "E427.MirrorCS", {"start": v(626.15, 165) * mm, "end": v(573.85, 165) * mm});
            skLineSegment(sketch, "E428.MirrorCS", {"start": v(616.15, 115) * mm, "end": v(616.15, 165) * mm});
            skLineSegment(sketch, "E429.MirrorCS", {"start": v(583.85, 115) * mm, "end": v(583.85, 165) * mm});
            skLineSegment(sketch, "E430.MirrorCS", {"start": v(616.15, 115) * mm, "end": v(583.85, 115) * mm});
            skLineSegment(sketch, "E431.MirrorCS", {"start": v(626.15, 115) * mm, "end": v(573.85, 115) * mm});
            skLineSegment(sketch, "E432.MirrorCS", {"start": v(583.85, -115) * mm, "end": v(583.85, -165) * mm});
            skLineSegment(sketch, "E433.MirrorCS", {"start": v(616.15, -115) * mm, "end": v(616.15, -165) * mm});
            skLineSegment(sketch, "E434.MirrorCS", {"start": v(616.15, -165) * mm, "end": v(583.85, -165) * mm});
            skLineSegment(sketch, "E435.MirrorCS", {"start": v(626.15, -165) * mm, "end": v(573.85, -165) * mm});
            skPoint(sketch, "E436.MirrorP", {"position": v(600, 140) * mm});
            skLineSegment(sketch, "E437.MirrorCS", {"start": v(626.15, -115) * mm, "end": v(626.15, -165) * mm});
            skPoint(sketch, "E438.MirrorP", {"position": v(600, -140) * mm});
            skLineSegment(sketch, "E439.MirrorCS", {"start": v(573.85, 115) * mm, "end": v(573.85, 165) * mm});
            skLineSegment(sketch, "E440.MirrorCS", {"start": v(626.15, 115) * mm, "end": v(626.15, 165) * mm});
            skLineSegment(sketch, "E441.MirrorCS", {"start": v(573.85, -115) * mm, "end": v(573.85, -165) * mm});
            skSolve(sketch);
        }
        {
            var Q0;
            Q0=makeQuery(id+"F36.imprint","IMPRINT",FACE,{"disambiguationData":[TD([[makeQuery(id+"F36.imprint","IMPRINT",EDGE,{"derivedFrom":sQuery(id+"F36.wireOp",EDGE,"E414.rect.bottom")}),-1.0]])]});
            var Q1;
            {var subQ1=sQuery(id+"F36.wireOp",EDGE,"E420.MirrorCS");Q1=makeQuery(id+"F36.imprint","IMPRINT",FACE,{"disambiguationData":[TD([[makeQuery(id+"F36.imprint","IMPRINT",EDGE,{"derivedFrom":subQ1}),1.0]])]});}
            var Q2;
            {var subQ2=sQuery(id+"F36.wireOp",EDGE,"E428.MirrorCS");Q2=makeQuery(id+"F36.imprint","IMPRINT",FACE,{"disambiguationData":[TD([[makeQuery(id+"F36.imprint","IMPRINT",EDGE,{"derivedFrom":subQ2}),1.0]])]});}
            var Q3;
            {var subQ2=sQuery(id+"F36.wireOp",EDGE,"E432.MirrorCS");Q3=makeQuery(id+"F36.imprint","IMPRINT",FACE,{"disambiguationData":[TD([[makeQuery(id+"F36.imprint","IMPRINT",EDGE,{"derivedFrom":subQ2}),1.0]])]});}
            extrude(context, id + "F37", {"entities" : qUnion([Q0, Q1, Q2, Q3]), "operationType" : NewBodyOperationType.ADD, "depth" : 25 * mm});
        }
        {
            var Q0;
            {var subQ1=sQuery(id+"F36.wireOp",EDGE,"E421.MirrorCS");Q0=makeQuery(id+"F36.imprint","IMPRINT",FACE,{"disambiguationData":[TD([[makeQuery(id+"F36.imprint","IMPRINT",EDGE,{"derivedFrom":subQ1}),1.0]])]});}
            var Q1;
            {var subQ2=sQuery(id+"F36.wireOp",EDGE,"E419.MirrorCS");Q1=makeQuery(id+"F36.imprint","IMPRINT",FACE,{"disambiguationData":[TD([[makeQuery(id+"F36.imprint","IMPRINT",EDGE,{"derivedFrom":subQ2}),1.0]])]});}
            var Q2;
            {var subQ1=sQuery(id+"F36.wireOp",EDGE,"E413.rect.left");Q2=makeQuery(id+"F36.imprint","IMPRINT",FACE,{"disambiguationData":[TD([[makeQuery(id+"F36.imprint","IMPRINT",EDGE,{"derivedFrom":subQ1}),1.0]])]});}
            var Q3;
            {var subQ1=sQuery(id+"F36.wireOp",EDGE,"E413.rect.right");Q3=makeQuery(id+"F36.imprint","IMPRINT",FACE,{"disambiguationData":[TD([[makeQuery(id+"F36.imprint","IMPRINT",EDGE,{"derivedFrom":subQ1}),-1.0]])]});}
            var Q4;
            {var subQ2=sQuery(id+"F36.wireOp",EDGE,"E429.MirrorCS");Q4=makeQuery(id+"F36.imprint","IMPRINT",FACE,{"disambiguationData":[TD([[makeQuery(id+"F36.imprint","IMPRINT",EDGE,{"derivedFrom":subQ2}),1.0]])]});}
            var Q5;
            {var subQ1=sQuery(id+"F36.wireOp",EDGE,"E428.MirrorCS");Q5=makeQuery(id+"F36.imprint","IMPRINT",FACE,{"disambiguationData":[TD([[makeQuery(id+"F36.imprint","IMPRINT",EDGE,{"derivedFrom":subQ1}),-1.0]])]});}
            var Q6;
            {var subQ2=sQuery(id+"F36.wireOp",EDGE,"E433.MirrorCS");Q6=makeQuery(id+"F36.imprint","IMPRINT",FACE,{"disambiguationData":[TD([[makeQuery(id+"F36.imprint","IMPRINT",EDGE,{"derivedFrom":subQ2}),1.0]])]});}
            var Q7;
            {var subQ2=sQuery(id+"F36.wireOp",EDGE,"E432.MirrorCS");Q7=makeQuery(id+"F36.imprint","IMPRINT",FACE,{"disambiguationData":[TD([[makeQuery(id+"F36.imprint","IMPRINT",EDGE,{"derivedFrom":subQ2}),-1.0]])]});}
            extrude(context, id + "F38", {"entities" : qUnion([Q0, Q1, Q2, Q3, Q4, Q5, Q6, Q7]), "operationType" : NewBodyOperationType.ADD, "depth" : 50 * mm});
        }
        {
            var Q0;
            Q0=makeQuery(id+"F1.opExtrude","SWEPT_EDGE",EDGE,{"disambiguationData":[OSD([sQuery(id+"F0.wireOp",EDGE,"E0.rect.top"),sQuery(id+"F0.wireOp",EDGE,"E0.rect.left")])]});
            var Q1;
            Q1=makeQuery(id+"F1.opExtrude","SWEPT_EDGE",EDGE,{"disambiguationData":[OSD([sQuery(id+"F0.wireOp",EDGE,"E0.rect.top"),sQuery(id+"F0.wireOp",EDGE,"E0.rect.right")])]});
            var Q2;
            Q2=makeQuery(id+"F1.opExtrude","SWEPT_EDGE",EDGE,{"disambiguationData":[OSD([sQuery(id+"F0.wireOp",EDGE,"E0.rect.bottom"),sQuery(id+"F0.wireOp",EDGE,"E0.rect.right")])]});
            var Q3;
            Q3=makeQuery(id+"F1.opExtrude","SWEPT_EDGE",EDGE,{"disambiguationData":[OSD([sQuery(id+"F0.wireOp",EDGE,"E0.rect.bottom"),sQuery(id+"F0.wireOp",EDGE,"E0.rect.left")])]});
            fillet(context, id + "F39", {"entities" : qUnion([Q0, Q1, Q2, Q3]), "radius" : 150 * mm, "tangentPropagation" : true, "allowEdgeOverflow" : false});
        }
    });
